FCSTD DOCUMENT  (FreeCAD 0.16R6712 (Git))
Label: randofo_robot_futaba_version
Comment: It has been modeled using a caliper and a real Futaba 3003 servo
License: CC-BY 3.0
LicenseURL: http://creativecommons.org/licenses/by/3.0/
objects: Part::Feature×186, Sketcher::SketchObject×36, PartDesign::Pocket×17, App::DocumentObjectGroup×13, Part::MultiFuse×12, PartDesign::Pad×10, Part::Fillet×4, Part::Cut×4, Mesh::Feature×4, Part::Loft×3, Part::Cylinder×3, Part::Extrusion×3, Part::Mirroring×2, Part::Compound×2, Part::Box×2, PartDesign::PolarPattern×1, PartDesign::Revolution×1, PartDesign::Fillet×1, PartDesign::Mirrored×1
note: 316 computed .brp shape members not serialized (recipe doc carries the construction recipe); baked Part::Feature solids carry a one-line shape summary decoded from their .brp

FEATURE [Sketcher::SketchObject] Sketch  label="body-sketch"
  Placement = pos=(0,0,0) rot=(1,0,0;1.5708rad)
  sketch-geometry (4):
    g0: LineSegment StartX=-20.15 StartY=36 StartZ=0 EndX=20.15 EndY=36 EndZ=0
    g1: LineSegment StartX=20.15 StartY=0 StartZ=0 EndX=-20.15 EndY=0 EndZ=0
    g2: LineSegment StartX=-20.15 StartY=0 StartZ=0 EndX=-20.15 EndY=36 EndZ=0
    g3: LineSegment StartX=20.15 StartY=36 StartZ=0 EndX=20.15 EndY=0 EndZ=0
  constraints (11):
    c: Coincident(g3,g1)
    c: Coincident(g1,g2)
    c: Horizontal(g0)
    c: Horizontal(g1)
    c: Vertical(g2)
    c: Symmetric(g0,g0,g-2)
    c: PointOnObject(g3,g-1)
    c: DistanceX(g0) = 40.3
    c: DistanceY(g0,g1) = -36
    c: Coincident(g2,g0)
    c: Coincident(g3,g0)
FEATURE [PartDesign::Pad] Pad  label="main_body"
  Length = 10
  Length2 = 100
  Placement = pos=(0,0,0) rot=(1,0,0;1.5708rad)
  Sketch = -> Sketch
  Type = 0
FEATURE [Sketcher::SketchObject] Sketch001  label="lateral-layer1-sketch"
  ExternalGeometry = -> [Pad]
  Placement = pos=(0,-10,0) rot=(1,0,0;1.5708rad)
  Support = -> Pad [Face14]
  sketch-geometry (6):
    g0: LineSegment StartX=20.15 StartY=33 StartZ=0 EndX=17.18 EndY=35.52 EndZ=0
    g1: LineSegment StartX=17.18 StartY=35.52 StartZ=0 EndX=-2.25 EndY=35.52 EndZ=0
    g2: LineSegment StartX=-2.25 StartY=35.52 StartZ=0 EndX=-20.15 EndY=33 EndZ=0
    g3: LineSegment StartX=-20.15 StartY=33 StartZ=0 EndX=-20.15 EndY=36 EndZ=0
    g4: LineSegment StartX=-20.15 StartY=36 StartZ=0 EndX=20.15 EndY=36 EndZ=0
    g5: LineSegment StartX=20.15 StartY=36 StartZ=0 EndX=20.15 EndY=33 EndZ=0
  constraints (16):
    c: Coincident(g0,g1)
    c: Horizontal(g1)
    c: Coincident(g1,g2)
    c: Coincident(g3,g2)
    c: Coincident(g4,g3)
    c: DistanceY(g0) = 33
    c: DistanceY(g4,g0) = -0.48
    c: DistanceX(g0,g0) = -2.97
    c: DistanceX(g4,g1) = -22.4
    c: Coincident(g5,g4)
    c: Coincident(g5,g0)
    c: PointOnObject(g0,g-4)
    c: Coincident(g4,g-4)
    c: Coincident(g3,g-3)
    c: PointOnObject(g2,g-3)
    c: DistanceY(g-1,g2) = 33
FEATURE [Sketcher::SketchObject] Sketch003
  Placement = pos=(0,0,0) rot=(0.57735,0.57735,0.57735;2.0944rad)
  sketch-geometry (4):
    g0: LineSegment StartX=-3.35 StartY=2.1 StartZ=0 EndX=3.35 EndY=2.1 EndZ=0
    g1: LineSegment StartX=3.35 StartY=2.1 StartZ=0 EndX=3.35 EndY=-2.1 EndZ=0
    g2: LineSegment StartX=3.35 StartY=-2.1 StartZ=0 EndX=-3.35 EndY=-2.1 EndZ=0
    g3: LineSegment StartX=-3.35 StartY=-2.1 StartZ=0 EndX=-3.35 EndY=2.1 EndZ=0
  constraints (12):
    c: Coincident(g0,g1)
    c: Coincident(g2,g3)
    c: Coincident(g3,g0)
    c: Horizontal(g0)
    c: Horizontal(g2)
    c: Vertical(g1)
    c: Vertical(g3)
    c: Symmetric(g0,g0,g-2)
    c: Coincident(g1,g2)
    c: DistanceY(g1) = -4.2
    c: DistanceX(g0) = 6.7
    c: Symmetric(g0,g2,g-1)
FEATURE [Sketcher::SketchObject] Sketch004
  Placement = pos=(1.8,0,0) rot=(0.57735,0.57735,0.57735;2.0944rad)
  sketch-geometry (4):
    g0: LineSegment StartX=-2.9 StartY=1.825 StartZ=0 EndX=2.9 EndY=1.825 EndZ=0
    g1: LineSegment StartX=2.9 StartY=1.825 StartZ=0 EndX=2.9 EndY=-1.825 EndZ=0
    g2: LineSegment StartX=2.9 StartY=-1.825 StartZ=0 EndX=-2.9 EndY=-1.825 EndZ=0
    g3: LineSegment StartX=-2.9 StartY=-1.825 StartZ=0 EndX=-2.9 EndY=1.825 EndZ=0
  constraints (12):
    c: Coincident(g0,g1)
    c: Coincident(g2,g3)
    c: Coincident(g3,g0)
    c: Horizontal(g0)
    c: Horizontal(g2)
    c: Vertical(g1)
    c: Vertical(g3)
    c: Symmetric(g0,g0,g-2)
    c: Coincident(g1,g2)
    c: DistanceY(g1) = -3.65
    c: DistanceX(g0) = 5.8
    c: Symmetric(g0,g2,g-1)
FEATURE [Part::Loft] Loft  label="wire-holder-body"
  Closed = false
  Placement = pos=(20.15,0,2.9) rot=(0,0,1;0rad)
  Ruled = false
  Sections = -> [Sketch003,Sketch004]
  Solid = true
FEATURE [Part::Cylinder] Cylinder  label="red-wire"
  Angle = 360
  Height = 10
  Placement = pos=(0,0,0) rot=(0,1,0;1.5708rad)
  Radius = 0.6
FEATURE [Part::Cylinder] Cylinder001  label="white-wire"
  Angle = 360
  Height = 10
  Placement = pos=(0,1.2,0) rot=(0,1,0;1.5708rad)
  Radius = 0.6
FEATURE [Part::Cylinder] Cylinder002  label="blck-wire"
  Angle = 360
  Height = 10
  Placement = pos=(0,-1.2,0) rot=(0,1,0;1.5708rad)
  Radius = 0.6
FEATURE [Sketcher::SketchObject] Sketch005
  ExternalGeometry = -> [Loft]
  Placement = pos=(21.95,0,2.9) rot=(0.57735,0.57735,0.57735;2.0944rad)
  Support = -> Loft [Face6]
  sketch-geometry (6):
    g0: LineSegment [constr] StartX=-1.2 StartY=0 StartZ=0 EndX=1.2 EndY=0 EndZ=0
    g1: ArcOfCircle CenterX=-1.2 CenterY=0 CenterZ=0 NormalX=0 NormalY=0 NormalZ=1 Radius=0.7 StartAngle=0.5411 EndAngle=5.74209
    g2: ArcOfCircle CenterX=0 CenterY=0 CenterZ=0 NormalX=0 NormalY=0 NormalZ=1 Radius=0.7 StartAngle=0.5411 EndAngle=2.60049
    g3: ArcOfCircle CenterX=0 CenterY=0 CenterZ=0 NormalX=0 NormalY=0 NormalZ=1 Radius=0.7 StartAngle=3.68269 EndAngle=5.74209
    g4: ArcOfCircle CenterX=1.2 CenterY=0 CenterZ=0 NormalX=0 NormalY=0 NormalZ=1 Radius=0.7 StartAngle=3.68269 EndAngle=8.88368
    g5: LineSegment [constr] StartX=-1.2 StartY=0 StartZ=0 EndX=-1.2 EndY=-0.7 EndZ=0
  constraints (20):
    c: Horizontal(g0)
    c: Symmetric(g0,g0,g-2)
    c: Coincident(g1,g0)
    c: PointOnObject(g2,g0)
    c: Coincident(g2,g1)
    c: PointOnObject(g2,g-2)
    c: Coincident(g3,g2)
    c: Coincident(g3,g1)
    c: Coincident(g4,g0)
    c: Coincident(g4,g2)
    c: Coincident(g4,g3)
    c: Equal(g1,g2)
    c: Equal(g2,g4)
    c: Equal(g4,g3)
    c: DistanceX(g2,g0) = 1.2
    c: Coincident(g5,g0)
    c: Vertical(g5)
    c: PointOnObject(g5,g1)
    c: Radius(g4) = 0.7
    c: PointOnObject(g0,g-1)
FEATURE [PartDesign::Pocket] Pocket002  label="wire-holder"
  Length = 1
  Placement = pos=(20.15,0,2.9) rot=(0,0,1;0rad)
  Sketch = -> Sketch005
  Type = 0
FEATURE [App::DocumentObjectGroup] Group  label="servo-wire-holder"
  Group = -> [Pocket002,Loft]
FEATURE [PartDesign::Pocket] Pocket  label="lateral-layer1"
  Length = 0.8
  Placement = pos=(0,0,0) rot=(1,0,0;1.5708rad)
  Sketch = -> Sketch001
  Type = 0
FEATURE [Sketcher::SketchObject] Sketch002  label="lateral-layer2-sketch"
  Placement = pos=(0,-9.2,0) rot=(1,0,0;1.5708rad)
  Support = -> Pocket [Face4]
  sketch-geometry (12):
    g0: GeomPoint [constr] X=19.55 Y=33.5091 Z=0
    g1: GeomPoint [constr] X=18.65 Y=36 Z=0
    g2: LineSegment StartX=18.65 StartY=36 StartZ=0 EndX=19.55 EndY=33.5091 EndZ=0
    g3: LineSegment StartX=19.55 StartY=33.5091 StartZ=0 EndX=20.15 EndY=33 EndZ=0
    g4: LineSegment StartX=18.65 StartY=36 StartZ=0 EndX=20.15 EndY=36 EndZ=0
    g5: LineSegment StartX=20.15 StartY=36 StartZ=0 EndX=20.15 EndY=33 EndZ=0
    g6: GeomPoint [constr] X=-16.9 Y=33.4575 Z=0
    g7: GeomPoint [constr] X=-13.35 Y=36 Z=0
    g8: LineSegment StartX=-20.15 StartY=33 StartZ=0 EndX=-16.9 EndY=33.4575 EndZ=0
    g9: LineSegment StartX=-16.9 StartY=33.4575 StartZ=0 EndX=-13.35 EndY=36 EndZ=0
    g10: LineSegment StartX=-20.15 StartY=33 StartZ=0 EndX=-20.15 EndY=36 EndZ=0
    g11: LineSegment StartX=-20.15 StartY=36 StartZ=0 EndX=-13.35 EndY=36 EndZ=0
  constraints (16):
    c: Coincident(g2,g1)
    c: Coincident(g2,g0)
    c: Coincident(g4,g1)
    c: Coincident(g5,g4)
    c: Coincident(g5,g3)
    c: Coincident(g3,g0)
    c: Coincident(g8,g6)
    c: Coincident(g9,g6)
    c: Coincident(g9,g7)
    c: DistanceX(g8,g6) = 3.25
    c: DistanceX(g7,g4) = 33.5
    c: Coincident(g10,g8)
    c: Coincident(g11,g10)
    c: Coincident(g11,g7)
    c: DistanceX(g4,g0) = -0.6
    c: DistanceX(g1,g4) = 1.5
FEATURE [PartDesign::Pocket] Pocket003  label="lateral-layer2"
  Length = 5
  Placement = pos=(0,0,0) rot=(1,0,0;1.5708rad)
  Sketch = -> Sketch002
  Type = 1
FEATURE [Part::Mirroring] Part__Mirroring  label="lateral-layer2 (Mirror #1)"
  Base = (0,0,0)
  Normal = (0,1,0)
  Source = -> Pocket003
FEATURE [Sketcher::SketchObject] Sketch006  label="ear-body-sketch"
  sketch-geometry (4):
    g0: LineSegment StartX=-27.75 StartY=9.05 StartZ=0 EndX=27.75 EndY=9.05 EndZ=0
    g1: LineSegment StartX=27.75 StartY=9.05 StartZ=0 EndX=27.75 EndY=-9.05 EndZ=0
    g2: LineSegment StartX=27.75 StartY=-9.05 StartZ=0 EndX=-27.75 EndY=-9.05 EndZ=0
    g3: LineSegment StartX=-27.75 StartY=-9.05 StartZ=0 EndX=-27.75 EndY=9.05 EndZ=0
  constraints (11):
    c: Coincident(g0,g1)
    c: Coincident(g1,g2)
    c: Coincident(g2,g3)
    c: Coincident(g3,g0)
    c: Horizontal(g0)
    c: Horizontal(g2)
    c: Vertical(g1)
    c: Vertical(g3)
    c: Symmetric(g0,g1,g-1)
    c: DistanceX(g0) = 55.5
    c: DistanceY(g1) = -18.1
FEATURE [PartDesign::Pad] Pad001  label="ear-body"
  Length = 2.6
  Length2 = 100
  Sketch = -> Sketch006
  Type = 0
FEATURE [Sketcher::SketchObject] Sketch007  label="ear-holes-sketch"
  Placement = pos=(0,0,2.6) rot=(0,0,1;0rad)
  Support = -> Pad001 [Face6]
  sketch-geometry (12):
    g0: Circle CenterX=-24.45 CenterY=5.05 CenterZ=0 NormalX=0 NormalY=0 NormalZ=1 Radius=2.15
    g1: Circle CenterX=-24.45 CenterY=-5.05 CenterZ=0 NormalX=0 NormalY=0 NormalZ=1 Radius=2.15
    g2: Circle CenterX=24.45 CenterY=5.05 CenterZ=0 NormalX=0 NormalY=0 NormalZ=1 Radius=2.15
    g3: Circle CenterX=24.45 CenterY=-5.05 CenterZ=0 NormalX=0 NormalY=0 NormalZ=1 Radius=2.15
    g4: LineSegment [constr] StartX=-24.45 StartY=5.05 StartZ=0 EndX=24.45 EndY=5.05 EndZ=0
    g5: LineSegment [constr] StartX=24.45 StartY=5.05 StartZ=0 EndX=24.45 EndY=-5.05 EndZ=0
    g6: LineSegment [constr] StartX=24.45 StartY=-5.05 StartZ=0 EndX=-24.45 EndY=-5.05 EndZ=0
    g7: LineSegment [constr] StartX=-24.45 StartY=-5.05 StartZ=0 EndX=-24.45 EndY=5.05 EndZ=0
    g8: GeomPoint [constr] X=-24.45 Y=2.9 Z=0
    g9: GeomPoint [constr] X=-22.3 Y=5.05 Z=0
    g10: GeomPoint [constr] X=-24.45 Y=-2.9 Z=0
    g11: GeomPoint [constr] X=22.3 Y=5.05 Z=0
  constraints (27):
    c: Coincident(g4,g5)
    c: Coincident(g5,g6)
    c: Coincident(g6,g7)
    c: Coincident(g7,g4)
    c: Horizontal(g4)
    c: Horizontal(g6)
    c: Vertical(g5)
    c: Vertical(g7)
    c: Symmetric(g4,g5,g-1)
    c: Coincident(g2,g4)
    c: Coincident(g3,g5)
    c: Coincident(g1,g6)
    c: Coincident(g0,g4)
    c: PointOnObject(g8,g7)
    c: PointOnObject(g9,g4)
    c: PointOnObject(g8,g0)
    c: PointOnObject(g9,g0)
    c: Equal(g0,g1)
    c: Equal(g1,g2)
    c: Equal(g2,g3)
    c: Radius(g0) = 2.15
    c: PointOnObject(g10,g7)
    c: PointOnObject(g10,g1)
    c: DistanceY(g8,g10) = -5.8
    c: PointOnObject(g11,g4)
    c: PointOnObject(g11,g2)
    c: DistanceX(g9,g11) = 44.6
FEATURE [PartDesign::Pocket] Pocket004  label="ear-holes"
  Length = 5
  Sketch = -> Sketch007
  Type = 1
FEATURE [Sketcher::SketchObject] Sketch008  label="nose-sketch"
  Placement = pos=(0,0,2.6) rot=(1,0,0;1.5708rad)
  sketch-geometry (6):
    g0: LineSegment StartX=-24.1 StartY=0 StartZ=0 EndX=-23.23 EndY=0.6 EndZ=0
    g1: LineSegment StartX=-23.23 StartY=0.6 StartZ=0 EndX=-20.15 EndY=1.5 EndZ=0
    g2: LineSegment StartX=-20.15 StartY=1.5 StartZ=0 EndX=20.15 EndY=1.5 EndZ=0
    g3: LineSegment StartX=20.15 StartY=1.5 StartZ=0 EndX=23.23 EndY=0.6 EndZ=0
    g4: LineSegment StartX=23.23 StartY=0.6 StartZ=0 EndX=24.1 EndY=0 EndZ=0
    g5: LineSegment StartX=24.1 StartY=0 StartZ=0 EndX=-24.1 EndY=0 EndZ=0
  constraints (17):
    c: PointOnObject(g0,g-1)
    c: Coincident(g0,g1)
    c: Coincident(g1,g2)
    c: Horizontal(g2)
    c: Coincident(g2,g3)
    c: Coincident(g3,g4)
    c: PointOnObject(g4,g-1)
    c: Coincident(g4,g5)
    c: Coincident(g5,g0)
    c: DistanceX(g2) = 40.3
    c: Symmetric(g1,g2,g-2)
    c: Symmetric(g3,g0,g-2)
    c: Symmetric(g0,g4,g-2)
    c: DistanceX(g0,g4) = 48.2
    c: DistanceX(g0,g1) = 3.08
    c: DistanceY(g0,g1) = 1.5
    c: DistanceY(g0,g0) = -0.6
FEATURE [PartDesign::Pad] Pad002  label="nose"
  Length = 1.5
  Length2 = 100
  Midplane = true
  Placement = pos=(0,0,2.6) rot=(1,0,0;1.5708rad)
  Sketch = -> Sketch008
  Type = 0
FEATURE [Sketcher::SketchObject] Sketch010
  sketch-geometry (1):
    g0: Circle CenterX=0 CenterY=0 CenterZ=0 NormalX=0 NormalY=0 NormalZ=1 Radius=7.2
  constraints (2):
    c: Coincident(g0,g-1)
    c: Radius(g0) = 7.2
FEATURE [Sketcher::SketchObject] Sketch011
  Placement = pos=(0,0,1.3) rot=(0,0,1;0rad)
  sketch-geometry (1):
    g0: Circle CenterX=0 CenterY=0 CenterZ=0 NormalX=0 NormalY=0 NormalZ=1 Radius=5.625
  constraints (2):
    c: Coincident(g0,g-1)
    c: Radius(g0) = 5.625
FEATURE [Part::Loft] Loft001  label="shaft-base1"
  Closed = false
  Placement = pos=(9.45,0,36) rot=(0,0,1;0rad)
  Ruled = false
  Sections = -> [Sketch010,Sketch011]
  Solid = true
FEATURE [Sketcher::SketchObject] Sketch012
  Placement = pos=(9.45,0,37.3) rot=(0,0,1;0rad)
  Support = -> Loft001 [Face3]
  sketch-geometry (1):
    g0: Circle CenterX=0 CenterY=0 CenterZ=0 NormalX=0 NormalY=0 NormalZ=1 Radius=4.95
  constraints (2):
    c: Coincident(g0,g-1)
    c: Radius(g0) = 4.95
FEATURE [PartDesign::Pad] Pad005  label="shaft-base2"
  Length = 0.2
  Length2 = 100
  Placement = pos=(9.45,0,36) rot=(0,0,1;0rad)
  Sketch = -> Sketch012
  Type = 0
FEATURE [Sketcher::SketchObject] Sketch013
  Placement = pos=(9.45,0,37.5) rot=(0,0,1;0rad)
  Support = -> Pad005 [Face5]
  sketch-geometry (1):
    g0: Circle CenterX=0 CenterY=0 CenterZ=0 NormalX=0 NormalY=0 NormalZ=1 Radius=3
  constraints (2):
    c: Coincident(g0,g-1)
    c: Radius(g0) = 3
FEATURE [PartDesign::Pad] Pad006  label="base-plus-basic-shaft"
  Length = 4.24
  Length2 = 100
  Placement = pos=(9.45,0,36) rot=(0,0,1;0rad)
  Sketch = -> Sketch013
  Type = 0
FEATURE [Sketcher::SketchObject] Sketch014  label="master-tooth-sketch"
  ExternalGeometry = -> [Pad006]
  Placement = pos=(9.45,0,41.74) rot=(0,0,1;0rad)
  Support = -> Pad006 [Face7]
  sketch-geometry (8):
    g0: Circle [constr] CenterX=0 CenterY=0 CenterZ=0 NormalX=0 NormalY=0 NormalZ=1 Radius=3.2
    g1: Circle [constr] CenterX=0 CenterY=0 CenterZ=0 NormalX=0 NormalY=0 NormalZ=1 Radius=2.8
    g2: LineSegment StartX=-0.1 StartY=3.19844 StartZ=0 EndX=0.1 EndY=3.19844 EndZ=0
    g3: LineSegment [constr] StartX=-0.1 StartY=3.19844 StartZ=0 EndX=0 EndY=0 EndZ=0
    g4: LineSegment [constr] StartX=0.1 StartY=3.19844 StartZ=0 EndX=0 EndY=0 EndZ=0
    g5: LineSegment StartX=-0.1 StartY=3.19844 StartZ=0 EndX=-0.0875 EndY=2.79863 EndZ=0
    g6: LineSegment StartX=-0.0875 StartY=2.79863 StartZ=0 EndX=0.0875 EndY=2.79863 EndZ=0
    g7: LineSegment StartX=0.0875 StartY=2.79863 StartZ=0 EndX=0.1 EndY=3.19844 EndZ=0
  constraints (20):
    c: Coincident(g0,g-1)
    c: Radius(g0) = 3.2
    c: Coincident(g1,g-1)
    c: Radius(g1) = 2.8
    c: Horizontal(g2)
    c: PointOnObject(g2,g0)
    c: PointOnObject(g2,g0)
    c: DistanceX(g2,g2) = 0.2
    c: Coincident(g3,g2)
    c: Coincident(g2,g4)
    c: Coincident(g4,g-1)
    c: Coincident(g3,g-1)
    c: Coincident(g5,g6)
    c: Coincident(g6,g7)
    c: Coincident(g5,g2)
    c: Coincident(g7,g2)
    c: PointOnObject(g5,g3)
    c: PointOnObject(g6,g4)
    c: PointOnObject(g5,g1)
    c: PointOnObject(g6,g1)
FEATURE [PartDesign::Pocket] Pocket005  label="master-tooth"
  Length = 4.1
  Placement = pos=(9.45,0,36) rot=(0,0,1;0rad)
  Sketch = -> Sketch014
  Type = 0
FEATURE [PartDesign::PolarPattern] PolarPattern  label="shaft-teeth"
  Angle = 360
  Axis = -> Sketch014 [N_Axis]
  Occurrences = 36
  Originals = -> [Pocket005]
  Placement = pos=(9.45,0,36) rot=(0,0,1;0rad)
FEATURE [Sketcher::SketchObject] Sketch017  label="top-cone-top"
  sketch-geometry (1):
    g0: Circle CenterX=0 CenterY=0 CenterZ=0 NormalX=0 NormalY=0 NormalZ=1 Radius=1.1
  constraints (2):
    c: Coincident(g0,g-1)
    c: Radius(g0) = 1.1
FEATURE [Sketcher::SketchObject] Sketch018  label="top-cone-bottom"
  Placement = pos=(0,0,0.6) rot=(0,0,1;0rad)
  sketch-geometry (1):
    g0: Circle CenterX=0 CenterY=0 CenterZ=0 NormalX=0 NormalY=0 NormalZ=1 Radius=1.25
  constraints (2):
    c: Coincident(g0,g-1)
    c: Radius(g0) = 1.25
FEATURE [Sketcher::SketchObject] Sketch021
  Placement = pos=(0,0,0) rot=(1,0,0;1.5708rad)
  sketch-geometry (6):
    g0: LineSegment StartX=0 StartY=0 StartZ=0 EndX=0.81 EndY=0 EndZ=0
    g1: LineSegment StartX=0.81 StartY=0 StartZ=0 EndX=0.81 EndY=27.6 EndZ=0
    g2: LineSegment StartX=0 StartY=28.9 StartZ=0 EndX=0 EndY=0 EndZ=0
    g3: LineSegment StartX=0.81 StartY=27.6 StartZ=0 EndX=1.65 EndY=27.6 EndZ=0
    g4: LineSegment StartX=1.65 StartY=27.6 StartZ=0 EndX=1.65 EndY=28.9 EndZ=0
    g5: LineSegment StartX=1.65 StartY=28.9 StartZ=0 EndX=0 EndY=28.9 EndZ=0
  constraints (17):
    c: Coincident(g0,g1)
    c: Coincident(g2,g0)
    c: Horizontal(g0)
    c: Vertical(g1)
    c: Vertical(g2)
    c: Coincident(g0,g-1)
    c: Coincident(g3,g4)
    c: Coincident(g4,g5)
    c: Coincident(g2,g5)
    c: Horizontal(g5)
    c: Coincident(g3,g1)
    c: Horizontal(g3)
    c: Vertical(g4)
    c: DistanceY(g2) = -28.9
    c: DistanceX(g0) = 0.81
    c: DistanceX(g5) = -1.65
    c: DistanceY(g4) = 1.3
FEATURE [PartDesign::Revolution] Revolution  label="screw-shape"
  Angle = 360
  Axis = (0,0,1)
  Base = (0,0,0)
  Placement = pos=(0,0,0) rot=(1,0,0;1.5708rad)
  ReferenceAxis = -> Sketch021 [V_Axis]
  Reversed = true
  Sketch = -> Sketch021
FEATURE [Sketcher::SketchObject] Sketch022  label="screw-cross-sketch"
  Placement = pos=(0,0,28.9) rot=(0,0,1;3.14159rad)
  Support = -> Revolution [Face5]
  sketch-geometry (12):
    g0: LineSegment StartX=-0.3 StartY=0.75 StartZ=0 EndX=0.3 EndY=0.75 EndZ=0
    g1: LineSegment StartX=0.3 StartY=0.75 StartZ=0 EndX=0.3 EndY=0.3 EndZ=0
    g2: LineSegment StartX=0.3 StartY=-0.75 StartZ=0 EndX=-0.3 EndY=-0.75 EndZ=0
    g3: LineSegment StartX=-0.3 StartY=-0.75 StartZ=0 EndX=-0.3 EndY=-0.3 EndZ=0
    g4: LineSegment StartX=-0.75 StartY=0.3 StartZ=0 EndX=-0.3 EndY=0.3 EndZ=0
    g5: LineSegment StartX=0.75 StartY=0.3 StartZ=0 EndX=0.75 EndY=-0.3 EndZ=0
    g6: LineSegment StartX=0.75 StartY=-0.3 StartZ=0 EndX=0.3 EndY=-0.3 EndZ=0
    g7: LineSegment StartX=-0.75 StartY=-0.3 StartZ=0 EndX=-0.75 EndY=0.3 EndZ=0
    g8: LineSegment StartX=-0.3 StartY=0.3 StartZ=0 EndX=-0.3 EndY=0.75 EndZ=0
    g9: LineSegment StartX=0.3 StartY=-0.3 StartZ=0 EndX=0.3 EndY=-0.75 EndZ=0
    g10: LineSegment StartX=0.3 StartY=0.3 StartZ=0 EndX=0.75 EndY=0.3 EndZ=0
    g11: LineSegment StartX=-0.3 StartY=-0.3 StartZ=0 EndX=-0.75 EndY=-0.3 EndZ=0
  constraints (30):
    c: Coincident(g0,g1)
    c: Coincident(g9,g2)
    c: Coincident(g2,g3)
    c: Coincident(g8,g0)
    c: Horizontal(g0)
    c: Horizontal(g2)
    c: Vertical(g1)
    c: Vertical(g3)
    c: Symmetric(g0,g9,g-1)
    c: Coincident(g10,g5)
    c: Coincident(g5,g6)
    c: Coincident(g11,g7)
    c: Coincident(g7,g4)
    c: Horizontal(g4)
    c: Horizontal(g6)
    c: Vertical(g5)
    c: Vertical(g7)
    c: Symmetric(g4,g5,g-1)
    c: Tangent(g3,g8)
    c: Tangent(g1,g9)
    c: Coincident(g4,g8)
    c: Coincident(g10,g1)
    c: Tangent(g4,g10)
    c: Coincident(g6,g9)
    c: Coincident(g11,g3)
    c: Tangent(g6,g11)
    c: Equal(g0,g7)
    c: Equal(g8,g4)
    c: DistanceX(g4,g5) = 1.5
    c: DistanceX(g0) = 0.6
FEATURE [PartDesign::Pocket] Pocket002006
  Length = 0.5
  Placement = pos=(0,0,0) rot=(1,0,0;1.5708rad)
  Sketch = -> Sketch022
  Type = 0
FEATURE [PartDesign::Fillet] Fillet  label="servo-screw-final1"
  Base = -> Pocket002006 [Edge5]
  Placement = pos=(0,0,0) rot=(1,0,0;1.5708rad)
  Radius = 0.4
FEATURE [Part::Feature] Fillet001  label="servo-screw1"
  Placement = pos=(17.6429,-7.49289,29) rot=(-1,0,0;1.5708rad)
  shape: bbox 3.572 x 3.572 x 28.9 mm, 19 faces (baked)
FEATURE [Part::Feature] Fillet001001  label="servo-screw002"
  Placement = pos=(-17.6429,-7.49289,29) rot=(-1,0,0;1.5708rad)
  shape: bbox 3.572 x 3.572 x 28.9 mm, 19 faces (baked)
FEATURE [Part::Feature] Fillet001002  label="servo-screw003"
  Placement = pos=(-17.6429,7.49289,29) rot=(-1,0,0;1.5708rad)
  shape: bbox 3.572 x 3.572 x 28.9 mm, 19 faces (baked)
FEATURE [Part::Feature] Fillet001003  label="servo-screw004"
  Placement = pos=(17.6429,7.49289,29) rot=(-1,0,0;1.5708rad)
  shape: bbox 3.572 x 3.572 x 28.9 mm, 19 faces (baked)
FEATURE [Sketcher::SketchObject] Sketch023
  Placement = pos=(9.45,0,41.74) rot=(0,0,1;0rad)
  Support = -> PolarPattern [Face9]
  sketch-geometry (1):
    g0: Circle CenterX=0 CenterY=0 CenterZ=0 NormalX=0 NormalY=0 NormalZ=1 Radius=0.9
  constraints (2):
    c: Coincident(g0,g-1)
    c: Radius(g0) = 0.9
FEATURE [PartDesign::Pocket] Pocket002007  label="shaft-drill-1"
  Length = 3
  Placement = pos=(9.45,0,36) rot=(0,0,1;0rad)
  Sketch = -> Sketch023
  Type = 0
FEATURE [Sketcher::SketchObject] Sketch024
  Placement = pos=(9.45,0,41.74) rot=(0,0,1;0rad)
  Support = -> Pocket002007 [Face9]
  sketch-geometry (1):
    g0: Circle CenterX=0 CenterY=0 CenterZ=0 NormalX=0 NormalY=0 NormalZ=1 Radius=1.15
  constraints (2):
    c: Coincident(g0,g-1)
    c: Radius(g0) = 1.15
FEATURE [PartDesign::Pocket] Pocket002008  label="shaft-drill-2"
  Length = 1
  Placement = pos=(9.45,0,36) rot=(0,0,1;0rad)
  Sketch = -> Sketch024
  Type = 0
FEATURE [App::DocumentObjectGroup] Group002  label="servo-shaft"
  Group = -> [Loft001,Pad005,Pad006,Pocket005,PolarPattern,Pocket002007,Pocket002008]
FEATURE [Part::Loft] Loft002  label="top-cone-master"
  Closed = false
  Placement = pos=(1,5.6,35.5) rot=(0,0,1;0rad)
  Ruled = false
  Sections = -> [Sketch017,Sketch018]
  Solid = true
FEATURE [Part::MultiFuse] Fusion006  label="servo-body001"
  Shapes = -> [Pocket003,Part__Mirroring]
FEATURE [Sketcher::SketchObject] Sketch015  label="top-details-1-sketch"
  ExternalGeometry = -> [Fusion006]
  Placement = pos=(0,0,36) rot=(0,0,1;0rad)
  Support = -> Fusion006 [Face8]
  sketch-geometry (10):
    g0: ArcOfCircle CenterX=-2.25 CenterY=0 CenterZ=0 NormalX=0 NormalY=0 NormalZ=1 Radius=1.7 StartAngle=4.71239 EndAngle=7.85398
    g1: LineSegment StartX=-2.25 StartY=9.2 StartZ=0 EndX=-2.25 EndY=1.7 EndZ=0
    g2: LineSegment StartX=-2.25 StartY=-1.7 StartZ=0 EndX=-2.25 EndY=-9.2 EndZ=0
    g3: ArcOfCircle CenterX=-2.25 CenterY=0 CenterZ=0 NormalX=0 NormalY=0 NormalZ=1 Radius=2.6 StartAngle=5.06586 EndAngle=7.50051
    g4: LineSegment [constr] StartX=-0.55 StartY=0 StartZ=0 EndX=0.35 EndY=0 EndZ=0
    g5: LineSegment [constr] StartX=-1.35 StartY=2.43926 StartZ=0 EndX=-2.25 EndY=2.43926 EndZ=0
    g6: LineSegment StartX=-1.35 StartY=2.43926 StartZ=0 EndX=-1.35 EndY=9.2 EndZ=0
    g7: LineSegment StartX=-2.25 StartY=9.2 StartZ=0 EndX=-1.35 EndY=9.2 EndZ=0
    g8: LineSegment StartX=-1.35 StartY=-2.43926 StartZ=0 EndX=-1.35 EndY=-9.2 EndZ=0
    g9: LineSegment StartX=-2.25 StartY=-9.2 StartZ=0 EndX=-1.35 EndY=-9.2 EndZ=0
  constraints (30):
    c: Radius(g0) = 1.7
    c: Symmetric(g0,g0,g-1)
    c: Coincident(g1,g0)
    c: Vertical(g1)
    c: Vertical(g2)
    c: Coincident(g2,g0)
    c: PointOnObject(g0,g1)
    c: Symmetric(g3,g3,g-1)
    c: PointOnObject(g4,g-1)
    c: Horizontal(g4)
    c: PointOnObject(g4,g0)
    c: PointOnObject(g4,g3)
    c: Coincident(g3,g0)
    c: DistanceX(g4) = 0.9
    c: Horizontal(g5)
    c: PointOnObject(g5,g1)
    c: Vertical(g6)
    c: Horizontal(g7)
    c: Coincident(g7,g1)
    c: Coincident(g7,g6)
    c: Coincident(g6,g3)
    c: DistanceX(g5) = -0.9
    c: Coincident(g5,g3)
    c: Coincident(g8,g3)
    c: Vertical(g8)
    c: Coincident(g9,g2)
    c: Horizontal(g9)
    c: Coincident(g9,g8)
    c: Symmetric(g1,g2,g-1)
    c: Coincident(g1,g-3)
FEATURE [PartDesign::Pocket] Pocket002008004  label="top-details-1"
  Length = 0.48
  Sketch = -> Sketch015
  Type = 0
FEATURE [Sketcher::SketchObject] Sketch016  label="top-details-2-sketch"
  ExternalGeometry = -> [Pocket002008004]
  Placement = pos=(0,0,36) rot=(0,0,1;0rad)
  Support = -> Pocket002008004 [Face21]
  sketch-geometry (6):
    g0: LineSegment StartX=-12.35 StartY=8.2 StartZ=0 EndX=-3.25 EndY=8.2 EndZ=0
    g1: LineSegment StartX=-3.25 StartY=8.2 StartZ=0 EndX=-3.25 EndY=-8.2 EndZ=0
    g2: LineSegment StartX=-3.25 StartY=-8.2 StartZ=0 EndX=-12.35 EndY=-8.2 EndZ=0
    g3: LineSegment StartX=-12.35 StartY=-8.2 StartZ=0 EndX=-12.35 EndY=8.2 EndZ=0
    g4: LineSegment [constr] StartX=-13.35 StartY=9.2 StartZ=0 EndX=-12.35 EndY=8.2 EndZ=0
    g5: LineSegment [constr] StartX=-2.25 StartY=-9.2 StartZ=0 EndX=-3.25 EndY=-8.2 EndZ=0
  constraints (16):
    c: Coincident(g4,g0)
    c: Coincident(g0,g3)
    c: Horizontal(g0)
    c: Vertical(g3)
    c: Coincident(g0,g1)
    c: Vertical(g1)
    c: Coincident(g2,g3)
    c: Horizontal(g2)
    c: Coincident(g1,g2)
    c: Coincident(g5,g1)
    c: DistanceX(g0,g4) = -1
    c: DistanceX(g5,g1) = -1
    c: Coincident(g4,g-3)
    c: Angle(g-3,g4) = 0.785398
    c: Coincident(g5,g-4)
    c: Angle(g5,g-1) = 0.785398
FEATURE [PartDesign::Pocket] Pocket002008007002  label="top-details-2"
  Length = 0.1
  Sketch = -> Sketch016
  Type = 0
FEATURE [Sketcher::SketchObject] Sketch025  label="bottom-details-1-sketch"
  ExternalGeometry = -> [Pocket002008007002]
  Placement = pos=(0,0,0) rot=(1,0,0;3.14159rad)
  Support = -> Pocket002008007002 [Face17]
  sketch-geometry (12):
    g0: LineSegment StartX=-17.6429 StartY=5.6 StartZ=0 EndX=-20.15 EndY=5.6 EndZ=0
    g1: LineSegment StartX=-20.15 StartY=5.6 StartZ=0 EndX=-20.15 EndY=10 EndZ=0
    g2: LineSegment StartX=-15.75 StartY=10 StartZ=0 EndX=-15.75 EndY=7.49289 EndZ=0
    g3: ArcOfCircle CenterX=-17.6429 CenterY=7.49289 CenterZ=0 NormalX=0 NormalY=0 NormalZ=1 Radius=1.89289 StartAngle=4.7124 EndAngle=6.28319
    g4: Circle [constr] CenterX=-17.6429 CenterY=7.49289 CenterZ=0 NormalX=0 NormalY=0 NormalZ=1 Radius=1
    g5: LineSegment StartX=-20.15 StartY=10 StartZ=0 EndX=-15.75 EndY=10 EndZ=0
    g6: LineSegment [constr] StartX=-20.15 StartY=10 StartZ=0 EndX=-18.35 EndY=8.2 EndZ=0
    g7: LineSegment StartX=-20.15 StartY=-5.6 StartZ=0 EndX=-20.15 EndY=-10 EndZ=0
    g8: LineSegment StartX=-20.15 StartY=-5.6 StartZ=0 EndX=-17.6429 EndY=-5.6 EndZ=0
    g9: LineSegment StartX=-20.15 StartY=-10 StartZ=0 EndX=-15.75 EndY=-10 EndZ=0
    g10: LineSegment StartX=-15.75 StartY=-10 StartZ=0 EndX=-15.75 EndY=-7.49289 EndZ=0
    g11: ArcOfCircle CenterX=-17.6429 CenterY=-7.49289 CenterZ=0 NormalX=0 NormalY=0 NormalZ=1 Radius=1.89289 StartAngle=6.28318 EndAngle=7.85397
  constraints (34):
    c: Coincident(g0,g1)
    c: Vertical(g2)
    c: Horizontal(g0)
    c: Vertical(g1)
    c: Coincident(g3,g2)
    c: Coincident(g3,g0)
    c: Tangent(g3,g0)
    c: Radius(g4) = 1
    c: Coincident(g3,g4)
    c: Coincident(g5,g1)
    c: Coincident(g5,g2)
    c: Horizontal(g5)
    c: Coincident(g6,g1)
    c: Angle(g6,g5) = 0.785398
    c: PointOnObject(g6,g4)
    c: PointOnObject(g3,g6)
    c: DistanceX(g5) = 4.4
    c: DistanceX(g6,g1) = -1.8
    c: Coincident(g1,g-3)
    c: Tangent(g2,g3)
    c: Vertical(g7)
    c: Symmetric(g7,g1,g-1)
    c: Symmetric(g7,g0,g-1)
    c: Horizontal(g8)
    c: Coincident(g8,g7)
    c: Symmetric(g8,g0,g-1)
    c: Horizontal(g9)
    c: Coincident(g9,g7)
    c: Symmetric(g9,g2,g-1)
    c: Coincident(g10,g9)
    c: Symmetric(g10,g2,g-1)
    c: Coincident(g11,g8)
    c: Coincident(g11,g10)
    c: Symmetric(g11,g3,g-1)
FEATURE [PartDesign::Pocket] Pocket002008007003  label="bottom-details-1"
  Length = 1.4
  Sketch = -> Sketch025
  Type = 0
FEATURE [PartDesign::Mirrored] Mirrored  label="bottom-details-1-complete"
  MirrorPlane = -> Sketch025 [V_Axis]
  Originals = -> [Pocket002008007003]
FEATURE [Sketcher::SketchObject] Sketch026  label="bottom-drills-sketch"
  ExternalGeometry = -> [Mirrored]
  Placement = pos=(0,0,0) rot=(1,0,0;3.14159rad)
  Support = -> Mirrored [Face19]
  sketch-geometry (6):
    g0: Circle CenterX=-17.6429 CenterY=7.49289 CenterZ=0 NormalX=0 NormalY=0 NormalZ=1 Radius=1
    g1: LineSegment [constr] StartX=-20.15 StartY=10 StartZ=0 EndX=-18.35 EndY=8.2 EndZ=0
    g2: LineSegment [constr] StartX=-20.15 StartY=10 StartZ=0 EndX=0 EndY=10 EndZ=0
    g3: Circle CenterX=-17.6429 CenterY=-7.49289 CenterZ=0 NormalX=0 NormalY=0 NormalZ=1 Radius=1
    g4: Circle CenterX=17.6429 CenterY=7.49289 CenterZ=0 NormalX=0 NormalY=0 NormalZ=1 Radius=1
    g5: Circle CenterX=17.6429 CenterY=-7.49289 CenterZ=0 NormalX=0 NormalY=0 NormalZ=1 Radius=1
  constraints (15):
    c: Radius(g0) = 1
    c: Coincident(g2,g1)
    c: Horizontal(g2)
    c: PointOnObject(g2,g-2)
    c: Angle(g1,g2) = 0.785398
    c: PointOnObject(g1,g0)
    c: PointOnObject(g0,g1)
    c: Coincident(g1,g-3)
    c: DistanceX(g1,g1) = -1.8
    c: Equal(g0,g3)
    c: Equal(g3,g5)
    c: Equal(g5,g4)
    c: Symmetric(g0,g3,g-1)
    c: Symmetric(g0,g4,g-2)
    c: Symmetric(g0,g5,g-1)
FEATURE [PartDesign::Pocket] Pocket002008007004  label="servo-body-final-1"
  Length = 30
  Sketch = -> Sketch026
  Type = 0
FEATURE [Part::Fillet] Fillet001007  label="servo-body-final-rounded"
  Base = -> Pocket002008007004
  Edges = 24 edges r=0.6: [Edge2,Edge5,Edge18,Edge24,Edge25,Edge26,Edge29,Edge30,Edge32,Edge33,Edge36,Edge39,Edge40,Edge41,Edge43,Edge46,Edge52,Edge53,Edge56,Edge59,Edge62,Edge77,Edge93,Edge95]
FEATURE [App::DocumentObjectGroup] Group005  label="servo-body"
  Group = -> [Pad,Pocket,Fusion006,Pocket002008004,Pocket002008007002,Pocket002008007003,Mirrored,Pocket002008007004,Fillet001007]
FEATURE [Part::MultiFuse] Fusion001  label="ears-final"
  Placement = pos=(0,0,25.8) rot=(0,0,1;0rad)
  Shapes = -> [Pocket004,Pad002]
FEATURE [Part::Fillet] Fillet001008  label="ears-final-rounded"
  Base = -> Fusion001
  Edges = 4 edges r=0.6: [Edge1,Edge2,Edge5,Edge8]
FEATURE [App::DocumentObjectGroup] Group001  label="servo-ears"
  Group = -> [Pad001,Pocket004,Pad002,Fusion001,Fillet001008]
FEATURE [Part::Feature] Fillet001007001  label="servo-body-1"
  shape: bbox 40.3 x 20 x 36.49 mm, 79 faces (baked)
FEATURE [Part::Mirroring] Part__Mirroring001  label="cone-2"
  Base = (0,0,0)
  Normal = (0,1,0)
  Source = -> Loft002
FEATURE [Part::MultiFuse] Fusion  label="two-top-cones"
  Shapes = -> [Loft002,Part__Mirroring001]
FEATURE [App::DocumentObjectGroup] Group006  label="top-cone"
  Group = -> [Loft002,Part__Mirroring001,Fusion]
FEATURE [Part::Feature] Fusion007  label="two-top-cones-1"
  shape: bbox 2.5 x 13.7 x 0.6 mm, 6 faces, 2 solids (baked)
FEATURE [Part::Cut] Cut  label="servo-body-2"
  Base = -> Fillet001007001
  Tool = -> Fusion007
FEATURE [Part::Feature] Pocket002008007005  label="servo-shaft-1"
  Placement = pos=(9.45,0,36) rot=(0,0,1;0rad)
  shape: bbox 14.4 x 14.4 x 5.74 mm, 155 faces (baked)
FEATURE [Part::Feature] Fillet001008001  label="servo-ears-1"
  shape: bbox 55.5 x 18.1 x 4.1 mm, 21 faces (baked)
FEATURE [Part::Feature] Pocket002008007006  label="Servo-wire-holder-1"
  Placement = pos=(20.15,0,2.9) rot=(0,0,1;0rad)
  shape: bbox 1.8 x 6.7 x 4.2 mm, 11 faces (baked)
FEATURE [Part::MultiFuse] Fusion008  label="Servo-no-screws"
  Shapes = -> [Cut,Fillet001008001,Pocket002008007006,Pocket002008007005]
FEATURE [Part::MultiFuse] Fusion009  label="servo-screws"
  Shapes = -> [Fillet001,Fillet001001,Fillet001002,Fillet001003]
FEATURE [App::DocumentObjectGroup] Group004  label="Servo-bottom-screws"
  Group = -> [Revolution,Pocket002006,Fillet,Fillet001,Fillet001001,Fillet001002,Fillet001003,Fusion009]
FEATURE [Part::Feature] Fusion009001  label="servo-screws-four"
  shape: bbox 38.86 x 18.56 x 28.9 mm, 76 faces, 4 solids (baked)
FEATURE [Part::MultiFuse] Fusion009002  label="Servo-Futaba3003-final"
  Shapes = -> [Fusion008,Fusion009001]
FEATURE [Part::MultiFuse] Fusion009003  label="servo-wires"
  Placement = pos=(20,0,2.9) rot=(0,0,1;0rad)
  Shapes = -> [Cylinder,Cylinder002,Cylinder001]
FEATURE [Part::Feature] Fusion009002001  label="Servo-Futaba3003-final001"
  shape: bbox 55.5 x 20 x 41.74 mm, 365 faces (baked)
FEATURE [Part::Feature] Fusion009003001  label="servo-wires001"
  Placement = pos=(20,0,2.9) rot=(0,0,1;0rad)
  shape: bbox 10 x 3.6 x 1.2 mm, 13 faces, 3 solids (baked)
FEATURE [Part::Compound] Compound  label="bottom-Futaba-3003-ready"
  Links = -> [Fusion009002001,Fusion009003001]
  Placement = pos=(31.103,29.7,25.8086) rot=(0,1,0;3.14159rad)
FEATURE [Part::Feature] FTTYB8MHZS8T52Z__1_001001_solid  label="FTTYB8MHZS8T52Z__1_002 (Solid)"
  shape: bbox 104.1 x 59.69 x 69.85 mm, 5828 faces (baked)
FEATURE [Part::Box] Box  label="Cubo"
  Height = 6.35
  Length = 55
  Placement = pos=(-158,79,0) rot=(0,0,1;0rad)
  Width = 20
FEATURE [Part::MultiFuse] Fusion009003002
  Shapes = -> [FTTYB8MHZS8T52Z__1_001001_solid,Box]
FEATURE [App::DocumentObjectGroup] Grupo  label="servo_futaba_components"
  Group = -> [Group,Group001,Group002,Group004,Group005,Group006,Fusion009002,Fusion009003]
FEATURE [Part::Compound] Compound001  label="front-Servo-Futaba-3003"
  Links = -> [Fusion009002001,Fusion009003001]
  Placement = pos=(54.5,29.8,38.4) rot=(0,1,0;1.5708rad)
FEATURE [Part::Box] Box001  label="Cubo001"
  Height = 57
  Length = 6.35
  Placement = pos=(-82.55,69.35,-59.6) rot=(0,0,1;0rad)
  Width = 40
FEATURE [Sketcher::SketchObject] Sketch029  label="futaba_hole001"
  Placement = pos=(95,118.75,168.7) rot=(0.707107,0,0.707107;3.14159rad)
  sketch-geometry (17):
    g0: Circle CenterX=-105.746 CenterY=94.0605 CenterZ=0 NormalX=0 NormalY=0 NormalZ=1 Radius=2.2
    g1: Circle CenterX=-105.746 CenterY=83.9412 CenterZ=0 NormalX=0 NormalY=0 NormalZ=1 Radius=2.2
    g2: Circle CenterX=-154.675 CenterY=83.9412 CenterZ=0 NormalX=0 NormalY=0 NormalZ=1 Radius=2.2
    g3: Circle CenterX=-154.675 CenterY=94.0605 CenterZ=0 NormalX=0 NormalY=0 NormalZ=1 Radius=2.2
    g4: LineSegment StartX=-150.836 StartY=99.4894 StartZ=0 EndX=-109.586 EndY=99.4894 EndZ=0
    g5: LineSegment StartX=-109.586 StartY=78.4894 StartZ=0 EndX=-150.836 EndY=78.4894 EndZ=0
    g6: LineSegment StartX=-150.836 StartY=78.4894 StartZ=0 EndX=-150.836 EndY=99.4894 EndZ=0
    g7: LineSegment StartX=-109.586 StartY=99.4894 StartZ=0 EndX=-109.586 EndY=93 EndZ=0
    g8: LineSegment StartX=-109.586 StartY=93 StartZ=0 EndX=-108 EndY=92 EndZ=0
    g9: LineSegment [constr] StartX=-158.75 StartY=89 StartZ=0 EndX=-108 EndY=89 EndZ=0
    g10: LineSegment StartX=-109.586 StartY=78.4894 StartZ=0 EndX=-109.586 EndY=85 EndZ=0
    g11: LineSegment StartX=-109.586 StartY=85 StartZ=0 EndX=-108 EndY=86 EndZ=0
    g12: LineSegment StartX=-108 StartY=86 StartZ=0 EndX=-108 EndY=87.529 EndZ=0
    g13: LineSegment StartX=-108 StartY=87.529 StartZ=0 EndX=-105.472 EndY=87.529 EndZ=0
    g14: LineSegment StartX=-108 StartY=92 StartZ=0 EndX=-108 EndY=90.4953 EndZ=0
    g15: LineSegment StartX=-108 StartY=90.4953 StartZ=0 EndX=-105.472 EndY=90.4953 EndZ=0
    g16: LineSegment StartX=-105.472 StartY=90.4953 StartZ=0 EndX=-105.472 EndY=87.529 EndZ=0
  constraints (35):
    c: Radius(g0) = 2.2
    c: Equal(g0,g1) = 2.2
    c: DistanceY(g1,g0) = 10.1193
    c: Equal(g0,g3) = 2.2
    c: Equal(g3,g2) = 2.2
    c: DistanceY(g2,g3) = 10.1193
    c: DistanceY(g3,g0) = 0
    c: DistanceX(g2,g3) = 0
    c: DistanceX(g3,g0) = 48.9287
    c: Coincident(g5,g6)
    c: Coincident(g6,g4)
    c: Horizontal(g4)
    c: Horizontal(g5)
    c: Vertical(g6)
    c: DistanceX(g5,g5) = 41.25
    c: DistanceY(g6,g6) = 21
    c: Coincident(g7,g4)
    c: Vertical(g7)
    c: Equal(g4,g5)
    c: Coincident(g7,g8)
    c: Horizontal(g9)
    c: Vertical(g10)
    c: Coincident(g10,g11)
    c: Coincident(g5,g10)
    c: Coincident(g12,g11)
    c: Vertical(g12)
    c: Coincident(g13,g12)
    c: Horizontal(g13)
    c: Coincident(g14,g8)
    c: Vertical(g14)
    c: Coincident(g15,g14)
    c: Horizontal(g15)
    c: Coincident(g16,g15)
    c: Coincident(g16,g13)
    c: Vertical(g16)
FEATURE [PartDesign::Pad] Pad007  label="servo_holes"
  Length = 10
  Length2 = 100
  Placement = pos=(95,118.75,168.7) rot=(0.707107,0,0.707107;3.14159rad)
  Reversed = true
  Sketch = -> Sketch029
  Type = 0
FEATURE [Part::Feature] Part__Feature524  label="Pcb007"
  Placement = pos=(-90.01,145.57,76.85) rot=(0,0,1;0rad)
  shape: bbox 68.58 x 53.34 x 1.6 mm, 170 faces (baked)
FEATURE [Part::Feature] Part__Feature525  label="LED_0603_009"
  Placement = pos=(9.41,44.13,76.85) rot=(0,0,1;0rad)
  shape: bbox 1.65 x 0.725 x 0.675 mm, 50 faces (baked)
FEATURE [Part::Feature] Part__Feature526  label="LED_0603_010"
  Placement = pos=(9.43,48.63,76.85) rot=(0,0,1;0rad)
  shape: bbox 1.65 x 0.725 x 0.675 mm, 50 faces (baked)
FEATURE [Part::Feature] Part__Feature527  label="1x10-socket-header_001"
  Placement = pos=(48.166,54.13,76.85) rot=(0,0,1;0rad)
  shape: bbox 25.4 x 2.54 x 11.85 mm, 186 faces (baked)
FEATURE [Part::Feature] Part__Feature528  label="1x6-male-pin-header-gray_002"
  Placement = pos=(53.5,15.395,76.85) rot=(0,0,1;3.14159rad)
  shape: bbox 15.24 x 2.54 x 11.2 mm, 210 faces (baked)
FEATURE [Part::Feature] Part__Feature529  label="1x8-socket-header_002"
  Placement = pos=(70.01,54.13,76.85) rot=(0,0,1;0rad)
  shape: bbox 20.32 x 2.54 x 11.85 mm, 150 faces (baked)
FEATURE [Part::Feature] Part__Feature530  label="1x8-male-pin-header_001"
  Placement = pos=(70.01,49.685,76.85) rot=(0,0,1;0rad)
  shape: bbox 20.32 x 2.54 x 11.2 mm, 278 faces (baked)
FEATURE [Part::Feature] Part__Feature531  label="1x6-male-pin-header-red_002"
  Placement = pos=(53.5,12.855,76.85) rot=(0,0,1;3.14159rad)
  shape: bbox 15.24 x 2.54 x 11.2 mm, 210 faces (baked)
FEATURE [Part::Feature] Part__Feature532  label="1x8-male-pin-header-red_001"
  Placement = pos=(70.01,47.145,76.85) rot=(0,0,1;0rad)
  shape: bbox 20.32 x 2.54 x 11.2 mm, 278 faces (baked)
FEATURE [Part::Feature] Part__Feature533  label="1x4-male-pin-header-red004_001"
  Placement = pos=(70.7085,27.9426,76.85) rot=(0,0,1;1.5708rad)
  shape: bbox 2.54 x 10.16 x 11.2 mm, 142 faces (baked)
FEATURE [Part::Feature] Part__Feature534  label="1x8-male-pin-header-gray_001"
  Placement = pos=(70.01,44.605,76.85) rot=(0,0,1;0rad)
  shape: bbox 20.32 x 2.54 x 11.2 mm, 278 faces (baked)
FEATURE [Part::Feature] Part__Feature535  label="1x8-socket-header_003"
  Placement = pos=(34.45,5.87,76.85) rot=(0,0,1;3.14159rad)
  shape: bbox 20.32 x 2.54 x 11.85 mm, 150 faces (baked)
FEATURE [Part::Feature] Part__Feature536  label="1x6-socket-header_001"
  Placement = pos=(57.31,5.87,76.85) rot=(0,0,1;3.14159rad)
  shape: bbox 15.24 x 2.54 x 11.85 mm, 114 faces (baked)
FEATURE [Part::Feature] Part__Feature537  label="SOT23-3_003"
  Placement = pos=(16.52,25.43,76.85) rot=(0,0,1;1.5708rad)
  shape: bbox 2.9 x 2.76 x 1.1 mm, 49 faces (baked)
FEATURE [Part::Feature] Part__Feature538  label="1x4-male-pin-header_001"
  Placement = pos=(73.2485,27.9426,76.85) rot=(0,0,1;1.5708rad)
  shape: bbox 2.54 x 10.16 x 11.2 mm, 142 faces (baked)
FEATURE [Part::Feature] Part__Feature539  label="SOT-563_001"
  Placement = pos=(14.0792,32.4384,76.85) rot=(0,0,1;3.14159rad)
  shape: bbox 1.6 x 1.6 x 0.55 mm, 48 faces (baked)
FEATURE [Part::Feature] Part__Feature540  label="1x4-male-pin-header-cyan_001"
  Placement = pos=(68.1685,27.9426,76.85) rot=(0,0,1;1.5708rad)
  shape: bbox 2.54 x 10.16 x 11.2 mm, 142 faces (baked)
FEATURE [Part::Feature] Part__Feature541  label="2x4-pin-header-yello_001"
  Placement = pos=(22.2961,21.1608,76.85) rot=(0,0,1;0rad)
  shape: bbox 10.16 x 5.08 x 11.2 mm, 271 faces (baked)
FEATURE [Part::Feature] Part__Feature542  label="USB-micro-B_001"
  Placement = pos=(8.48,32.25,76.85) rot=(0,0,1;0rad)
  shape: bbox 5.438 x 7.977 x 2.937 mm, 448 faces (baked)
FEATURE [Part::Feature] Part__Feature543  label="slide-sw-right-angle_001"
  Placement = pos=(27.6047,8.537,76.85) rot=(0,0,1;0rad)
  shape: bbox 10 x 7.561 x 5.5 mm, 95 faces (baked)
FEATURE [Part::Feature] Part__Feature544  label="SOT23-3_004"
  Placement = pos=(9.21,21.82,76.85) rot=(0,0,1;0rad)
  shape: bbox 2.76 x 2.9 x 1.1 mm, 49 faces (baked)
FEATURE [Part::Feature] Part__Feature545  label="LED_0603_011"
  Placement = pos=(9.41,45.63,76.85) rot=(0,0,1;0rad)
  shape: bbox 1.65 x 0.725 x 0.675 mm, 50 faces (baked)
FEATURE [Part::Feature] Part__Feature546  label="R_Array_4x0603_002"
  Placement = pos=(13.4696,46.4211,76.85) rot=(0,0,1;3.14159rad)
  shape: bbox 1.62 x 3.498 x 0.5525 mm, 95 faces (baked)
FEATURE [Part::Feature] Part__Feature547  label="LED_0603_012"
  Placement = pos=(9.41,53.13,76.85) rot=(0,0,1;0rad)
  shape: bbox 1.65 x 0.725 x 0.675 mm, 50 faces (baked)
FEATURE [Part::Feature] Part__Feature548  label="sw_smd_6.0x3.8_002"
  Placement = pos=(23.61,47.53,76.85) rot=(0,0,1;0rad)
  shape: bbox 3.899 x 7.3 x 2.5 mm, 90 faces (baked)
FEATURE [Part::Feature] Part__Feature549  label="1x6-pin-header_002"
  Placement = pos=(48.166,49.685,76.85) rot=(0,0,1;0rad)
  shape: bbox 15.24 x 2.54 x 11.2 mm, 210 faces (baked)
FEATURE [Part::Feature] Part__Feature550  label="PVQFN20_002"
  Placement = pos=(62.5043,20.4369,76.85) rot=(0,0,1;3.14159rad)
  shape: bbox 4.52 x 3.52 x 0.9 mm, 133 faces (baked)
FEATURE [Part::Feature] Part__Feature551  label="1x6-pin-header_003"
  Placement = pos=(53.5,10.315,76.85) rot=(0,0,1;3.14159rad)
  shape: bbox 15.24 x 2.54 x 11.2 mm, 210 faces (baked)
FEATURE [Part::Feature] Part__Feature552  label="LED_0603_013"
  Placement = pos=(9.41,54.63,76.85) rot=(0,0,1;0rad)
  shape: bbox 1.65 x 0.725 x 0.675 mm, 50 faces (baked)
FEATURE [Part::Feature] Part__Feature553  label="1x6-male-pin-header-red_003"
  Placement = pos=(48.166,47.145,76.85) rot=(0,0,1;0rad)
  shape: bbox 15.24 x 2.54 x 11.2 mm, 210 faces (baked)
FEATURE [Part::Feature] Part__Feature554  label="LED_0603_014"
  Placement = pos=(9.41,51.63,76.85) rot=(0,0,1;0rad)
  shape: bbox 1.65 x 0.725 x 0.675 mm, 50 faces (baked)
FEATURE [Part::Feature] Part__Feature555  label="1x6-male-pin-header-gray_003"
  Placement = pos=(48.166,44.605,76.85) rot=(0,0,1;0rad)
  shape: bbox 15.24 x 2.54 x 11.2 mm, 210 faces (baked)
FEATURE [Part::Feature] Part__Feature556  label="LED_0603_015"
  Placement = pos=(9.41,47.13,76.85) rot=(0,0,1;0rad)
  shape: bbox 1.65 x 0.725 x 0.675 mm, 50 faces (baked)
FEATURE [Part::Feature] Part__Feature557  label="LED_0603_016"
  Placement = pos=(9.41,50.13,76.85) rot=(0,0,1;0rad)
  shape: bbox 1.65 x 0.725 x 0.675 mm, 50 faces (baked)
FEATURE [Part::Feature] Part__Feature558  label="R_Array_4x0603_003"
  Placement = pos=(13.4696,51.9964,76.85) rot=(0,0,1;3.14159rad)
  shape: bbox 1.62 x 3.498 x 0.5525 mm, 95 faces (baked)
FEATURE [Part::Feature] Part__Feature559  label="LED_0603_017"
  Placement = pos=(33.0022,10.061,76.85) rot=(0,0,1;0rad)
  shape: bbox 1.65 x 0.725 x 0.675 mm, 50 faces (baked)
FEATURE [Part::Feature] Part__Feature560  label="sw_smd_6.0x3.8_003"
  Placement = pos=(18.21,47.53,76.85) rot=(0,0,1;0rad)
  shape: bbox 3.899 x 7.3 x 2.5 mm, 90 faces (baked)
FEATURE [Part::Feature] Part__Feature561  label="PVQFN20_003"
  Placement = pos=(63.0758,38.7122,76.85) rot=(0,0,1;0rad)
  shape: bbox 4.52 x 3.52 x 0.9 mm, 133 faces (baked)
FEATURE [Part::Feature] Part__Feature562  label="SOT23-3_005"
  Placement = pos=(9.21,25.44,76.85) rot=(0,0,1;0rad)
  shape: bbox 2.76 x 2.9 x 1.1 mm, 49 faces (baked)
FEATURE [Part::Feature] Part__Feature563  label="C_0402_053"
  Placement = pos=(33.4467,36.4262,76.85) rot=(0,0,1;1.5708rad)
  shape: bbox 0.5 x 0.985 x 0.5 mm, 44 faces (baked)
FEATURE [Part::Feature] Part__Feature564  label="MSOP-8_001"
  Placement = pos=(22.9438,39.7917,76.85) rot=(0,0,1;0rad)
  shape: bbox 5.141 x 3.2 x 1 mm, 115 faces (baked)
FEATURE [Part::Feature] Part__Feature565  label="xtal-3_2x2_5_001"
  Placement = pos=(16.2509,38.8265,76.85) rot=(0,0,1;0rad)
  shape: bbox 2.5 x 3.2 x 0.92 mm, 29 faces (baked)
FEATURE [Part::Feature] Part__Feature566  label="F1812-505k_001"
  Placement = pos=(10.28,41.09,76.85) rot=(0,0,1;3.14159rad)
  shape: bbox 4.73 x 3.41 x 1.39 mm, 94 faces (baked)
FEATURE [Part::Feature] Part__Feature567  label="jack_DC_2.1mm_PCB_001"
  Placement = pos=(11.9202,11.6866,76.85) rot=(0,0,-1;1.5708rad)
  shape: bbox 14.5 x 9.46 x 14.8 mm, 34 faces (baked)
FEATURE [Part::Feature] Part__Feature568  label="DO-214AC_001"
  Placement = pos=(10.7772,18.2398,76.85) rot=(0,0,1;3.14159rad)
  shape: bbox 5.475 x 2.8 x 2.574 mm, 39 faces (baked)
FEATURE [Part::Feature] Part__Feature569  label="SOD-323_002"
  Placement = pos=(13.3426,26.8504,76.85) rot=(0,0,1;0rad)
  shape: bbox 2.6 x 1.35 x 1.113 mm, 38 faces (baked)
FEATURE [Part::Feature] Part__Feature570  label="DFN-2523-6_003"
  Placement = pos=(20.6832,18.2652,76.85) rot=(0,0,-1;1.5708rad)
  shape: bbox 2.4 x 2.5 x 0.62 mm, 44 faces (baked)
FEATURE [Part::Feature] Part__Feature571  label="DFN-2523-6_004"
  Placement = pos=(16.3398,18.2271,76.85) rot=(0,0,1;1.5708rad)
  shape: bbox 2.4 x 2.5 x 0.62 mm, 44 faces (baked)
FEATURE [Part::Feature] Part__Feature572  label="C_0402_054"
  Placement = pos=(27.6047,46.8275,76.85) rot=(0,0,-1;1.5708rad)
  shape: bbox 0.5 x 0.985 x 0.5 mm, 44 faces (baked)
FEATURE [Part::Feature] Part__Feature573  label="DFN-2523-6_005"
  Placement = pos=(40.9016,9.934,76.85) rot=(0,0,-1;1.5708rad)
  shape: bbox 2.4 x 2.5 x 0.62 mm, 44 faces (baked)
FEATURE [Part::Feature] Part__Feature574  label="PVQFN16_001"
  Placement = pos=(31.28,45.82,76.85) rot=(0,0,1;0rad)
  shape: bbox 4.17 x 3.7 x 1.1 mm, 109 faces (baked)
FEATURE [Part::Feature] Part__Feature575  label="C_0402_055"
  Placement = pos=(66.1111,21.2243,76.85) rot=(0,0,1;1.5708rad)
  shape: bbox 0.5 x 0.985 x 0.5 mm, 44 faces (baked)
FEATURE [Part::Feature] Part__Feature576  label="L_4040_001"
  Placement = pos=(32.7609,14.9505,76.85) rot=(0,0,-1;1.5708rad)
  shape: bbox 4.3 x 4.3 x 2.33 mm, 122 faces (baked)
FEATURE [Part::Feature] Part__Feature577  label="QFN16_002"
  Placement = pos=(62.7837,29.5174,76.85) rot=(0,0,1;0rad)
  shape: bbox 3.08 x 3.08 x 0.9 mm, 118 faces (baked)
FEATURE [Part::Feature] Part__Feature578  label="QFN16_003"
  Placement = pos=(27.9222,15.3569,76.85) rot=(0,0,1;3.14159rad)
  shape: bbox 3.08 x 3.08 x 0.9 mm, 118 faces (baked)
FEATURE [Part::Feature] Part__Feature579  label="C_0402_056"
  Placement = pos=(12.1996,38.2042,76.85) rot=(0,0,1;3.14159rad)
  shape: bbox 0.985 x 0.5 x 0.5 mm, 44 faces (baked)
FEATURE [Part::Feature] Part__Feature580  label="FTDI-QFN-64_001"
  Placement = pos=(23.0581,31.4732,76.85) rot=(0,0,1;0rad)
  shape: bbox 9.04 x 9.04 x 0.95 mm, 849 faces (baked)
FEATURE [Part::Feature] Part__Feature581  label="C_0402_057"
  Placement = pos=(30.3098,50.3327,76.85) rot=(0,0,1;1.5708rad)
  shape: bbox 0.5 x 0.985 x 0.5 mm, 44 faces (baked)
FEATURE [Part::Feature] Part__Feature582  label="C_0402_058"
  Placement = pos=(16.8097,29.7333,76.85) rot=(0,0,1;3.14159rad)
  shape: bbox 0.985 x 0.5 x 0.5 mm, 44 faces (baked)
FEATURE [Part::Feature] Part__Feature583  label="C_0402_059"
  Placement = pos=(59.6087,39.8298,76.85) rot=(0,0,-1;1.5708rad)
  shape: bbox 0.5 x 0.985 x 0.5 mm, 44 faces (baked)
FEATURE [Part::Feature] Part__Feature584  label="C_1206_002"
  Placement = pos=(28.1762,10.9627,76.85) rot=(0,0,1;3.14159rad)
  shape: bbox 3.2 x 1.6 x 1 mm, 44 faces (baked)
FEATURE [Part::Feature] Part__Feature585  label="C_0402_060"
  Placement = pos=(29.2938,12.601,76.85) rot=(0,0,1;3.14159rad)
  shape: bbox 0.985 x 0.5 x 0.5 mm, 44 faces (baked)
FEATURE [Part::Feature] Part__Feature586  label="C_0402_061"
  Placement = pos=(33.3197,50.3327,76.85) rot=(0,0,1;1.5708rad)
  shape: bbox 0.5 x 0.985 x 0.5 mm, 44 faces (baked)
FEATURE [Part::Feature] Part__Feature587  label="C_0402_062"
  Placement = pos=(33.0022,25.7201,76.85) rot=(0,0,1;3.14159rad)
  shape: bbox 0.985 x 0.5 x 0.5 mm, 44 faces (baked)
FEATURE [Part::Feature] Part__Feature588  label="C_0603_014"
  Placement = pos=(26.8046,18.6335,76.85) rot=(0,0,1;0rad)
  shape: bbox 1.6 x 0.8 x 0.6 mm, 44 faces (baked)
FEATURE [Part::Feature] Part__Feature589  label="C_0402_063"
  Placement = pos=(26.6141,46.8275,76.85) rot=(0,0,1;1.5708rad)
  shape: bbox 0.5 x 0.985 x 0.5 mm, 44 faces (baked)
FEATURE [Part::Feature] Part__Feature590  label="C_0402_064"
  Placement = pos=(31.31,50.33,76.85) rot=(0,0,1;1.5708rad)
  shape: bbox 0.5 x 0.985 x 0.5 mm, 44 faces (baked)
FEATURE [Part::Feature] Part__Feature591  label="DFN-3030-8_001"
  Placement = pos=(37.3202,16.1062,76.85) rot=(0,0,1;3.14159rad)
  shape: bbox 3.02 x 3 x 0.85 mm, 89 faces (baked)
FEATURE [Part::Feature] Part__Feature592  label="C_0603_015"
  Placement = pos=(29.6113,18.3287,76.85) rot=(0,0,1;0rad)
  shape: bbox 1.6 x 0.8 x 0.6 mm, 44 faces (baked)
FEATURE [Part::Feature] Part__Feature593  label="C_0402_065"
  Placement = pos=(16.8097,30.635,76.85) rot=(0,0,1;0rad)
  shape: bbox 0.985 x 0.5 x 0.5 mm, 44 faces (baked)
FEATURE [Part::Feature] Part__Feature594  label="C_0402_066"
  Placement = pos=(47.6707,17.5159,76.85) rot=(0,0,1;0rad)
  shape: bbox 0.985 x 0.5 x 0.5 mm, 44 faces (baked)
FEATURE [Part::Feature] Part__Feature595  label="C_0402_067"
  Placement = pos=(43.7083,17.5286,76.85) rot=(0,0,1;3.14159rad)
  shape: bbox 0.985 x 0.5 x 0.5 mm, 44 faces (baked)
FEATURE [Part::Feature] Part__Feature596  label="C_0402_068"
  Placement = pos=(20.353,25.7582,76.85) rot=(0,0,1;3.14159rad)
  shape: bbox 0.985 x 0.5 x 0.5 mm, 44 faces (baked)
FEATURE [Part::Feature] Part__Feature597  label="C_0402_069"
  Placement = pos=(22.8549,37.1755,76.85) rot=(0,0,1;3.14159rad)
  shape: bbox 0.985 x 0.5 x 0.5 mm, 44 faces (baked)
FEATURE [Part::Feature] Part__Feature598  label="C_0402_070"
  Placement = pos=(58.199,28.5268,76.85) rot=(0,0,-1;1.5708rad)
  shape: bbox 0.5 x 0.985 x 0.5 mm, 44 faces (baked)
FEATURE [Part::Feature] Part__Feature599  label="C_0603_016"
  Placement = pos=(32.5069,21.6307,76.85) rot=(0,0,1;1.5708rad)
  shape: bbox 0.8 x 1.6 x 0.6 mm, 44 faces (baked)
FEATURE [Part::Feature] Part__Feature600  label="C_0402_071"
  Placement = pos=(63.7108,42.3317,76.85) rot=(0,0,1;0rad)
  shape: bbox 0.985 x 0.5 x 0.5 mm, 44 faces (baked)
FEATURE [Part::Feature] Part__Feature601  label="C_0603_017"
  Placement = pos=(16.5938,35.7404,76.85) rot=(0,0,1;3.14159rad)
  shape: bbox 1.6 x 0.8 x 0.6 mm, 44 faces (baked)
FEATURE [Part::Feature] Part__Feature602  label="pushbutton-right-angle_001"
  Placement = pos=(72.169,20.221,76.85) rot=(0,0,1;1.5708rad)
  shape: bbox 7.9 x 7.4 x 11 mm, 130 faces (baked)
FEATURE [Part::Feature] Part__Feature603  label="C_0402_072"
  Placement = pos=(27.6047,44.1351,76.85) rot=(0,0,-1;1.5708rad)
  shape: bbox 0.5 x 0.985 x 0.5 mm, 44 faces (baked)
FEATURE [Part::Feature] Part__Feature604  label="C_0402_073"
  Placement = pos=(27.1729,25.7328,76.85) rot=(0,0,1;0rad)
  shape: bbox 0.985 x 0.5 x 0.5 mm, 44 faces (baked)
FEATURE [Part::Feature] Part__Feature605  label="C_0402_074"
  Placement = pos=(59.6087,37.62,76.85) rot=(0,0,-1;1.5708rad)
  shape: bbox 0.5 x 0.985 x 0.5 mm, 44 faces (baked)
FEATURE [Part::Feature] Part__Feature606  label="WSON-6_001"
  Placement = pos=(38.2854,12.728,76.85) rot=(0,0,1;0rad)
  shape: bbox 1.6 x 1.55 x 0.85 mm, 44 faces (baked)
FEATURE [Part::Feature] Part__Feature607  label="C_0402_075"
  Placement = pos=(56.8782,19.2304,76.85) rot=(0,0,-1;1.5708rad)
  shape: bbox 0.5 x 0.985 x 0.5 mm, 44 faces (baked)
FEATURE [Part::Feature] Part__Feature608  label="TQFP-144_001"
  Placement = pos=(45.9308,30,76.85) rot=(0,0,1;0rad)
  shape: bbox 21.98 x 21.98 x 1.12 mm, 2168 faces (baked)
FEATURE [Part::Feature] Part__Feature609  label="C_0603_018"
  Placement = pos=(40.1142,12.9058,76.85) rot=(0,0,-1;1.5708rad)
  shape: bbox 0.8 x 1.6 x 0.6 mm, 44 faces (baked)
FEATURE [Part::Feature] Part__Feature610  label="C_0402_076"
  Placement = pos=(19.1084,39.9314,76.85) rot=(0,0,1;1.5708rad)
  shape: bbox 0.5 x 0.985 x 0.5 mm, 44 faces (baked)
FEATURE [Part::Feature] Part__Feature611  label="C_0603_019"
  Placement = pos=(21.8008,14.9378,76.85) rot=(0,0,-1;1.5708rad)
  shape: bbox 0.8 x 1.6 x 0.6 mm, 44 faces (baked)
FEATURE [Part::Feature] Part__Feature612  label="C_0402_077"
  Placement = pos=(66.2,42.319,76.85) rot=(0,0,1;3.14159rad)
  shape: bbox 0.985 x 0.5 x 0.5 mm, 44 faces (baked)
FEATURE [Part::Feature] Part__Feature613  label="C_0402_078"
  Placement = pos=(68.7146,42.3317,76.85) rot=(0,0,1;0rad)
  shape: bbox 0.985 x 0.5 x 0.5 mm, 44 faces (baked)
FEATURE [Part::Feature] Part__Feature614  label="C_0402_079"
  Placement = pos=(28.3032,50.3327,76.85) rot=(0,0,1;1.5708rad)
  shape: bbox 0.5 x 0.985 x 0.5 mm, 44 faces (baked)
FEATURE [Part::Feature] Part__Feature615  label="L_0603_003"
  Placement = pos=(12.5044,36.0325,76.85) rot=(0,0,1;1.5708rad)
  shape: bbox 0.8 x 1.6 x 0.6 mm, 44 faces (baked)
FEATURE [Part::Feature] Part__Feature616  label="C_0402_080"
  Placement = pos=(26.0934,37.1374,76.85) rot=(0,0,1;3.14159rad)
  shape: bbox 0.985 x 0.5 x 0.5 mm, 44 faces (baked)
FEATURE [Part::Feature] Part__Feature617  label="C_0603_020"
  Placement = pos=(10.0533,38.2042,76.85) rot=(0,0,1;0rad)
  shape: bbox 1.6 x 0.8 x 0.6 mm, 44 faces (baked)
FEATURE [Part::Feature] Part__Feature618  label="C_0402_081"
  Placement = pos=(58.199,35.4229,76.85) rot=(0,0,1;1.5708rad)
  shape: bbox 0.5 x 0.985 x 0.5 mm, 44 faces (baked)
FEATURE [Part::Feature] Part__Feature619  label="R_0402_037"
  Placement = pos=(16.797,33.6322,76.85) rot=(0,0,1;0rad)
  shape: bbox 1 x 0.5 x 0.3 mm, 40 faces (baked)
FEATURE [Part::Feature] Part__Feature620  label="C_0402_082"
  Placement = pos=(29.2049,32.2352,76.85) rot=(0,0,1;0rad)
  shape: bbox 0.985 x 0.5 x 0.5 mm, 44 faces (baked)
FEATURE [Part::Feature] Part__Feature621  label="C_0402_083"
  Placement = pos=(32.3037,50.3327,76.85) rot=(0,0,1;1.5708rad)
  shape: bbox 0.5 x 0.985 x 0.5 mm, 44 faces (baked)
FEATURE [Part::Feature] Part__Feature622  label="C_0603_021"
  Placement = pos=(66.0095,33.429,76.85) rot=(0,0,1;1.5708rad)
  shape: bbox 0.8 x 1.6 x 0.6 mm, 44 faces (baked)
FEATURE [Part::Feature] Part__Feature623  label="C_1206_003"
  Placement = pos=(23.8963,13.49,76.85) rot=(0,0,-1;1.5708rad)
  shape: bbox 1.6 x 3.2 x 1 mm, 44 faces (baked)
FEATURE [Part::Feature] Part__Feature624  label="C_0603_022"
  Placement = pos=(14.2316,30.3429,76.85) rot=(0,0,1;3.14159rad)
  shape: bbox 1.6 x 0.8 x 0.6 mm, 44 faces (baked)
FEATURE [Part::Feature] Part__Feature625  label="C_0402_084"
  Placement = pos=(19.21,37.2898,76.85) rot=(0,0,1;3.14159rad)
  shape: bbox 0.985 x 0.5 x 0.5 mm, 44 faces (baked)
FEATURE [Part::Feature] Part__Feature626  label="C_0603_023"
  Placement = pos=(12.6568,20.729,76.85) rot=(0,0,1;0rad)
  shape: bbox 1.6 x 0.8 x 0.6 mm, 44 faces (baked)
FEATURE [Part::Feature] Part__Feature627  label="C_0402_085"
  Placement = pos=(26.61,44.13,76.85) rot=(0,0,-1;1.5708rad)
  shape: bbox 0.5 x 0.985 x 0.5 mm, 44 faces (baked)
FEATURE [Part::Feature] Part__Feature628  label="SOD-323_003"
  Placement = pos=(58.32,38.1,76.85) rot=(0,0,-1;1.5708rad)
  shape: bbox 1.35 x 2.6 x 1.113 mm, 38 faces (baked)
FEATURE [Part::Feature] Part__Feature629  label="DFN-8-6x5mm_001"
  Placement = pos=(47.61,13.9,76.85) rot=(0,0,1;3.14159rad)
  shape: bbox 6.1 x 5 x 0.9466 mm, 62 faces (baked)
FEATURE [Part::Feature] Part__Feature630  label="C_0402_086"
  Placement = pos=(28.8112,29.1364,76.85) rot=(0,0,-1;1.5708rad)
  shape: bbox 0.5 x 0.985 x 0.5 mm, 44 faces (baked)
FEATURE [Part::Feature] Part__Feature631  label="L_0603_004"
  Placement = pos=(14.4856,35.1054,76.85) rot=(0,0,1;1.5708rad)
  shape: bbox 0.8 x 1.6 x 0.6 mm, 44 faces (baked)
FEATURE [Part::Feature] Part__Feature632  label="C_0402_087"
  Placement = pos=(58.2117,31.524,76.85) rot=(0,0,1;1.5708rad)
  shape: bbox 0.5 x 0.985 x 0.5 mm, 44 faces (baked)
FEATURE [Part::Feature] Part__Feature633  label="C_0603_024"
  Placement = pos=(19.0068,22.5832,76.85) rot=(0,0,-1;1.5708rad)
  shape: bbox 0.8 x 1.6 x 0.6 mm, 44 faces (baked)
FEATURE [Part::Feature] Part__Feature634  label="C_0603_025"
  Placement = pos=(39.9999,16.6523,76.85) rot=(0,0,1;1.5708rad)
  shape: bbox 0.8 x 1.6 x 0.6 mm, 44 faces (baked)
FEATURE [Part::Feature] Part__Feature635  label="R_0402_038"
  Placement = pos=(29.8145,40.5283,76.85) rot=(0,0,1;1.5708rad)
  shape: bbox 0.5 x 1 x 0.3 mm, 40 faces (baked)
FEATURE [Part::Feature] Part__Feature636  label="C_0402_088"
  Placement = pos=(61.1073,42.3317,76.85) rot=(0,0,1;3.14159rad)
  shape: bbox 0.985 x 0.5 x 0.5 mm, 44 faces (baked)
FEATURE [Part::Feature] Part__Feature637  label="C_0402_089"
  Placement = pos=(33.0022,24.2342,76.85) rot=(0,0,1;3.14159rad)
  shape: bbox 0.985 x 0.5 x 0.5 mm, 44 faces (baked)
FEATURE [Part::Feature] Part__Feature638  label="C_0402_090"
  Placement = pos=(33.6118,21.4275,76.85) rot=(0,0,1;1.5708rad)
  shape: bbox 0.5 x 0.985 x 0.5 mm, 44 faces (baked)
FEATURE [Part::Feature] Part__Feature639  label="L_0603_005"
  Placement = pos=(23.909,16.9317,76.85) rot=(0,0,1;0rad)
  shape: bbox 1.6 x 0.8 x 0.6 mm, 44 faces (baked)
FEATURE [Part::Feature] Part__Feature640  label="C_0603_026"
  Placement = pos=(28.735,35.3721,76.85) rot=(0,0,-1;1.5708rad)
  shape: bbox 0.8 x 1.6 x 0.6 mm, 44 faces (baked)
FEATURE [Part::Feature] Part__Feature641  label="C_0402_091"
  Placement = pos=(66.1111,19.332,76.85) rot=(0,0,1;1.5708rad)
  shape: bbox 0.5 x 0.985 x 0.5 mm, 44 faces (baked)
FEATURE [Part::Feature] Part__Feature642  label="L_0805_001"
  Placement = pos=(13.6728,28.8824,76.85) rot=(0,0,1;0rad)
  shape: bbox 2 x 1.25 x 1.25 mm, 50 faces (baked)
FEATURE [Part::Feature] Part__Feature643  label="C_0402_092"
  Placement = pos=(29.3065,50.3327,76.85) rot=(0,0,1;1.5708rad)
  shape: bbox 0.5 x 0.985 x 0.5 mm, 44 faces (baked)
FEATURE [Part::Feature] Part__Feature644  label="C_0402_093"
  Placement = pos=(16.797,34.6228,76.85) rot=(0,0,1;3.14159rad)
  shape: bbox 0.985 x 0.5 x 0.5 mm, 44 faces (baked)
FEATURE [Part::Feature] Part__Feature645  label="R_0402_039"
  Placement = pos=(26.8046,40.5283,76.85) rot=(0,0,1;1.5708rad)
  shape: bbox 0.5 x 1 x 0.3 mm, 40 faces (baked)
FEATURE [Part::Feature] Part__Feature646  label="C_0402_094"
  Placement = pos=(71.3054,42.3317,76.85) rot=(0,0,1;3.14159rad)
  shape: bbox 0.985 x 0.5 x 0.5 mm, 44 faces (baked)
FEATURE [Part::Feature] Part__Feature647  label="C_0402_095"
  Placement = pos=(16.7081,41.3665,76.85) rot=(0,0,1;3.14159rad)
  shape: bbox 0.985 x 0.5 x 0.5 mm, 44 faces (baked)
FEATURE [Part::Feature] Part__Feature648  label="C_0402_096"
  Placement = pos=(42.9082,12.5375,76.85) rot=(0,0,1;1.5708rad)
  shape: bbox 0.5 x 0.985 x 0.5 mm, 44 faces (baked)
FEATURE [Part::Feature] Part__Feature649  label="C_0402_097"
  Placement = pos=(41.7652,17.1349,76.85) rot=(0,0,-1;1.5708rad)
  shape: bbox 0.5 x 0.985 x 0.5 mm, 44 faces (baked)
FEATURE [Part::Feature] Part__Feature650  label="C_0402_098"
  Placement = pos=(63.5076,32.3368,76.85) rot=(0,0,1;3.14159rad)
  shape: bbox 0.985 x 0.5 x 0.5 mm, 44 faces (baked)
FEATURE [Part::Feature] Part__Feature651  label="C_0402_099"
  Placement = pos=(61.6153,32.3368,76.85) rot=(0,0,1;3.14159rad)
  shape: bbox 0.985 x 0.5 x 0.5 mm, 44 faces (baked)
FEATURE [Part::Feature] Part__Feature652  label="C_0603_027"
  Placement = pos=(41.3207,12.9058,76.85) rot=(0,0,-1;1.5708rad)
  shape: bbox 0.8 x 1.6 x 0.6 mm, 44 faces (baked)
FEATURE [Part::Feature] Part__Feature653  label="C_0402_100"
  Placement = pos=(58.6054,42.3317,76.85) rot=(0,0,1;0rad)
  shape: bbox 0.985 x 0.5 x 0.5 mm, 44 faces (baked)
FEATURE [Part::Feature] Part__Feature654  label="C_0402_101"
  Placement = pos=(56.0019,42.3317,76.85) rot=(0,0,1;0rad)
  shape: bbox 0.985 x 0.5 x 0.5 mm, 44 faces (baked)
FEATURE [Part::Feature] Part__Feature655  label="C_0402_102"
  Placement = pos=(53.4111,42.3317,76.85) rot=(0,0,1;3.14159rad)
  shape: bbox 0.985 x 0.5 x 0.5 mm, 44 faces (baked)
FEATURE [Part::Feature] Part__Feature656  label="C_0402_103"
  Placement = pos=(47.0738,42.3317,76.85) rot=(0,0,1;3.14159rad)
  shape: bbox 0.985 x 0.5 x 0.5 mm, 44 faces (baked)
FEATURE [Part::Feature] Part__Feature657  label="C_0402_104"
  Placement = pos=(50.706,42.3317,76.85) rot=(0,0,1;3.14159rad)
  shape: bbox 0.985 x 0.5 x 0.5 mm, 44 faces (baked)
FEATURE [Part::Feature] Part__Feature658  label="C_0402_105"
  Placement = pos=(42.0319,42.4333,76.85) rot=(0,0,1;0rad)
  shape: bbox 0.985 x 0.5 x 0.5 mm, 44 faces (baked)
FEATURE [Part::Feature] Part__Feature659  label="R_0402_040"
  Placement = pos=(28.8112,40.5283,76.85) rot=(0,0,-1;1.5708rad)
  shape: bbox 0.5 x 1 x 0.3 mm, 40 faces (baked)
FEATURE [Part::Feature] Part__Feature660  label="R_0402_041"
  Placement = pos=(27.8079,40.5283,76.85) rot=(0,0,-1;1.5708rad)
  shape: bbox 0.5 x 1 x 0.3 mm, 40 faces (baked)
FEATURE [Part::Feature] Part__Feature661  label="R_0402_042"
  Placement = pos=(16.81,28.33,76.85) rot=(0,0,1;0rad)
  shape: bbox 1 x 0.5 x 0.3 mm, 40 faces (baked)
FEATURE [Part::Feature] Part__Feature662  label="R_0402_043"
  Placement = pos=(14.2062,25.0343,76.85) rot=(0,0,1;1.5708rad)
  shape: bbox 0.5 x 1 x 0.3 mm, 40 faces (baked)
FEATURE [Part::Feature] Part__Feature663  label="R_0402_044"
  Placement = pos=(12.5044,25.5296,76.85) rot=(0,0,1;3.14159rad)
  shape: bbox 1 x 0.5 x 0.3 mm, 40 faces (baked)
FEATURE [Part::Feature] Part__Feature664  label="R_0402_045"
  Placement = pos=(12.5044,24.539,76.85) rot=(0,0,1;3.14159rad)
  shape: bbox 1 x 0.5 x 0.3 mm, 40 faces (baked)
FEATURE [Part::Feature] Part__Feature665  label="R_0402_046"
  Placement = pos=(16.9113,22.3292,76.85) rot=(0,0,1;3.14159rad)
  shape: bbox 1 x 0.5 x 0.3 mm, 40 faces (baked)
FEATURE [Part::Feature] Part__Feature666  label="R_0402_047"
  Placement = pos=(14.9047,20.729,76.85) rot=(0,0,1;3.14159rad)
  shape: bbox 1 x 0.5 x 0.3 mm, 40 faces (baked)
FEATURE [Part::Feature] Part__Feature667  label="R_0402_048"
  Placement = pos=(15.0063,22.3292,76.85) rot=(0,0,1;3.14159rad)
  shape: bbox 1 x 0.5 x 0.3 mm, 40 faces (baked)
FEATURE [Part::Feature] Part__Feature668  label="R_0402_049"
  Placement = pos=(16.797,20.729,76.85) rot=(0,0,1;0rad)
  shape: bbox 1 x 0.5 x 0.3 mm, 40 faces (baked)
FEATURE [Part::Feature] Part__Feature669  label="R_0402_050"
  Placement = pos=(33.8023,8.4227,76.85) rot=(0,0,1;1.5708rad)
  shape: bbox 0.5 x 1 x 0.3 mm, 40 faces (baked)
FEATURE [Part::Feature] Part__Feature670  label="R_0402_051"
  Placement = pos=(18.702,20.729,76.85) rot=(0,0,1;0rad)
  shape: bbox 1 x 0.5 x 0.3 mm, 40 faces (baked)
FEATURE [Part::Feature] Part__Feature671  label="R_0402_052"
  Placement = pos=(33.0022,19.7257,76.85) rot=(0,0,1;3.14159rad)
  shape: bbox 1 x 0.5 x 0.3 mm, 40 faces (baked)
FEATURE [Part::Feature] Part__Feature672  label="R_0402_053"
  Placement = pos=(33.0022,28.73,76.85) rot=(0,0,1;0rad)
  shape: bbox 1 x 0.5 x 0.3 mm, 40 faces (baked)
FEATURE [Part::Feature] Part__Feature673  label="R_0402_054"
  Placement = pos=(36.3042,12.728,76.85) rot=(0,0,-1;1.5708rad)
  shape: bbox 0.5 x 1 x 0.3 mm, 40 faces (baked)
FEATURE [Part::Feature] Part__Feature674  label="R_0402_055"
  Placement = pos=(50.706,17.5286,76.85) rot=(0,0,1;3.14159rad)
  shape: bbox 1 x 0.5 x 0.3 mm, 40 faces (baked)
FEATURE [Part::Feature] Part__Feature675  label="R_0402_056"
  Placement = pos=(36.7106,11.0262,76.85) rot=(0,0,1;3.14159rad)
  shape: bbox 1 x 0.5 x 0.3 mm, 40 faces (baked)
FEATURE [Part::Feature] Part__Feature676  label="R_0402_057"
  Placement = pos=(58.707,23.1293,76.85) rot=(0,0,1;0rad)
  shape: bbox 1 x 0.5 x 0.3 mm, 40 faces (baked)
FEATURE [Part::Feature] Part__Feature677  label="R_0402_058"
  Placement = pos=(36.7106,10.0356,76.85) rot=(0,0,1;3.14159rad)
  shape: bbox 1 x 0.5 x 0.3 mm, 40 faces (baked)
FEATURE [Part::Feature] Part__Feature678  label="R_0402_059"
  Placement = pos=(47.2135,9.9213,76.85) rot=(0,0,1;1.5708rad)
  shape: bbox 0.5 x 1 x 0.3 mm, 40 faces (baked)
FEATURE [Part::Feature] Part__Feature679  label="R_0402_060"
  Placement = pos=(46.2102,9.9213,76.85) rot=(0,0,1;1.5708rad)
  shape: bbox 0.5 x 1 x 0.3 mm, 40 faces (baked)
FEATURE [Part::Feature] Part__Feature680  label="R_0402_061"
  Placement = pos=(48.2041,9.9213,76.85) rot=(0,0,1;1.5708rad)
  shape: bbox 0.5 x 1 x 0.3 mm, 40 faces (baked)
FEATURE [Part::Feature] Part__Feature681  label="R_0402_062"
  Placement = pos=(68.2066,12.2327,76.85) rot=(0,0,-1;1.5708rad)
  shape: bbox 0.5 x 1 x 0.3 mm, 40 faces (baked)
FEATURE [Part::Feature] Part__Feature682  label="R_0402_063"
  Placement = pos=(49.2074,9.9213,76.85) rot=(0,0,1;1.5708rad)
  shape: bbox 0.5 x 1 x 0.3 mm, 40 faces (baked)
FEATURE [Part::Feature] Part__Feature683  label="R_0402_064"
  Placement = pos=(68.2066,10.1245,76.85) rot=(0,0,1;1.5708rad)
  shape: bbox 0.5 x 1 x 0.3 mm, 40 faces (baked)
FEATURE [Part::Feature] Part__Feature684  label="R_0402_065"
  Placement = pos=(67.3049,21.2243,76.85) rot=(0,0,1;1.5708rad)
  shape: bbox 0.5 x 1 x 0.3 mm, 40 faces (baked)
FEATURE [Part::Feature] Part__Feature685  label="R_0402_066"
  Placement = pos=(59.9008,28.1331,76.85) rot=(0,0,-1;1.5708rad)
  shape: bbox 0.5 x 1 x 0.3 mm, 40 faces (baked)
FEATURE [Part::Feature] Part__Feature686  label="R_0402_067"
  Placement = pos=(67.3049,19.332,76.85) rot=(0,0,-1;1.5708rad)
  shape: bbox 0.5 x 1 x 0.3 mm, 40 faces (baked)
FEATURE [Part::Feature] Part__Feature687  label="R_0402_068"
  Placement = pos=(66,35.63,76.85) rot=(0,0,1;1.5708rad)
  shape: bbox 0.5 x 1 x 0.3 mm, 40 faces (baked)
FEATURE [Part::Feature] Part__Feature688  label="R_0402_069"
  Placement = pos=(59.9008,31.1303,76.85) rot=(0,0,1;1.5708rad)
  shape: bbox 0.5 x 1 x 0.3 mm, 40 faces (baked)
FEATURE [Part::Feature] Part__Feature689  label="R_0402_070"
  Placement = pos=(12.5044,23.523,76.85) rot=(0,0,1;0rad)
  shape: bbox 1 x 0.5 x 0.3 mm, 40 faces (baked)
FEATURE [Part::Feature] Part__Feature690  label="R_0402_071"
  Placement = pos=(12.5044,22.3292,76.85) rot=(0,0,1;3.14159rad)
  shape: bbox 1 x 0.5 x 0.3 mm, 40 faces (baked)
FEATURE [Part::Feature] Part__Feature691  label="R_0402_072"
  Placement = pos=(23.2105,25.7328,76.85) rot=(0,0,1;3.14159rad)
  shape: bbox 1 x 0.5 x 0.3 mm, 40 faces (baked)
FEATURE [Part::Feature] Part__Feature692  label="R_0402_073"
  Placement = pos=(25.1028,25.7328,76.85) rot=(0,0,1;0rad)
  shape: bbox 1 x 0.5 x 0.3 mm, 40 faces (baked)
FEATURE [Part::Feature] Part__Feature693  label="1x3-pin-header_001"
  Placement = pos=(68.0796,37.6581,76.85) rot=(0,0,-1;1.5708rad)
  shape: bbox 2.54 x 7.62 x 11.2 mm, 108 faces (baked)
FEATURE [Part::Feature] Part__Feature694  label="jumper-cap-2.54mm_001"
  Placement = pos=(68.0796,37.6581,76.85) rot=(0,0,1;1.5708rad)
  shape: bbox 2.5 x 5 x 6 mm, 108 faces (baked)
FEATURE [App::DocumentObjectGroup] Grupo028  label="step001"
  Group = -> [Part__Feature524,Part__Feature525,Part__Feature526,Part__Feature527,Part__Feature528,Part__Feature529,Part__Feature530,Part__Feature531,Part__Feature532,Part__Feature533,Part__Feature534,Part__Feature535,Part__Feature536,Part__Feature537,Part__Feature538,Part__Feature539,Part__Feature540,Part__Feature541,Part__Feature542,Part__Feature543,Part__Feature544,Part__Feature545,Part__Feature546,+148 more]
FEATURE [App::DocumentObjectGroup] Grupo027  label="icezum_alhambra001"
  Group = -> [Grupo028]
FEATURE [Sketcher::SketchObject] Sketch030  label="futaba_hole002"
  Placement = pos=(-260.45,178,-2) rot=(0,0,1;3.14159rad)
  sketch-geometry (14):
    g0: Circle CenterX=-105.746 CenterY=94.0605 CenterZ=0 NormalX=0 NormalY=0 NormalZ=1 Radius=2.2
    g1: Circle CenterX=-105.746 CenterY=83.9412 CenterZ=0 NormalX=0 NormalY=0 NormalZ=1 Radius=2.2
    g2: Circle CenterX=-154.675 CenterY=83.9412 CenterZ=0 NormalX=0 NormalY=0 NormalZ=1 Radius=2.2
    g3: Circle CenterX=-154.675 CenterY=94.0605 CenterZ=0 NormalX=0 NormalY=0 NormalZ=1 Radius=2.2
    g4: LineSegment StartX=-150.836 StartY=99.4894 StartZ=0 EndX=-109.586 EndY=99.4894 EndZ=0
    g5: LineSegment StartX=-109.586 StartY=78.4894 StartZ=0 EndX=-150.836 EndY=78.4894 EndZ=0
    g6: LineSegment StartX=-150.836 StartY=78.4894 StartZ=0 EndX=-150.836 EndY=99.4894 EndZ=0
    g7: LineSegment StartX=-109.586 StartY=99.4894 StartZ=0 EndX=-109.586 EndY=93 EndZ=0
    g8: LineSegment StartX=-109.586 StartY=93 StartZ=0 EndX=-108 EndY=92 EndZ=0
    g9: LineSegment StartX=-108 StartY=92 StartZ=0 EndX=-108 EndY=89 EndZ=0
    g10: LineSegment [constr] StartX=-158.75 StartY=89 StartZ=0 EndX=-108 EndY=89 EndZ=0
    g11: LineSegment StartX=-109.586 StartY=78.4894 StartZ=0 EndX=-109.586 EndY=85 EndZ=0
    g12: LineSegment StartX=-109.586 StartY=85 StartZ=0 EndX=-108 EndY=86 EndZ=0
    g13: LineSegment StartX=-108 StartY=86 StartZ=0 EndX=-108 EndY=89 EndZ=0
  constraints (30):
    c: Radius(g0) = 2.2
    c: Equal(g0,g1) = 2.2
    c: DistanceY(g1,g0) = 10.1193
    c: Equal(g0,g3) = 2.2
    c: Equal(g3,g2) = 2.2
    c: DistanceY(g2,g3) = 10.1193
    c: DistanceY(g3,g0) = 0
    c: DistanceX(g2,g3) = 0
    c: DistanceX(g3,g0) = 48.9287
    c: Coincident(g5,g6)
    c: Coincident(g6,g4)
    c: Horizontal(g4)
    c: Horizontal(g5)
    c: Vertical(g6)
    c: DistanceX(g5,g5) = 41.25
    c: DistanceY(g6,g6) = 21
    c: Coincident(g7,g4)
    c: Vertical(g7)
    c: Equal(g4,g5)
    c: Coincident(g7,g8)
    c: Coincident(g8,g9)
    c: Vertical(g9)
    c: Coincident(g10,g9)
    c: Horizontal(g10)
    c: Vertical(g11)
    c: Coincident(g11,g12)
    c: Coincident(g12,g13)
    c: Vertical(g13)
    c: Coincident(g5,g11)
    c: Coincident(g9,g13)
FEATURE [PartDesign::Pad] Pad008  label="servo_holes001"
  Length = 10
  Length2 = 100
  Placement = pos=(-260.45,178,-2) rot=(0,0,1;3.14159rad)
  Sketch = -> Sketch030
  Type = 0
FEATURE [Part::MultiFuse] Fusion009003003  label="body_without_servo_holes"
  Shapes = -> [Fusion009003002,Box001]
FEATURE [Part::MultiFuse] Fusion009003004  label="servo_holes002"
  Shapes = -> [Pad007,Pad008]
FEATURE [Part::Cut] Cut001  label="robot_futaba_body"
  Base = -> Fusion009003003
  Placement = pos=(161.5,118.9,6.5) rot=(1,0,0;3.14159rad)
  Tool = -> Fusion009003004
FEATURE [Sketcher::SketchObject] Sketch032
  Placement = pos=(161.5,118.5,63.65) rot=(0,0,1;0rad)
  sketch-geometry (4):
    g0: LineSegment StartX=-161.284 StartY=-60.5356 StartZ=0 EndX=-80.7406 EndY=-60.5356 EndZ=0
    g1: LineSegment StartX=-80.7406 StartY=-60.5356 StartZ=0 EndX=-80.7406 EndY=-116.4 EndZ=0
    g2: LineSegment StartX=-80.7406 StartY=-116.4 StartZ=0 EndX=-161.284 EndY=-116.4 EndZ=0
    g3: LineSegment StartX=-161.284 StartY=-116.4 StartZ=0 EndX=-161.284 EndY=-60.5356 EndZ=0
  constraints (8):
    c: Coincident(g0,g1)
    c: Coincident(g1,g2)
    c: Coincident(g2,g3)
    c: Coincident(g3,g0)
    c: Horizontal(g0)
    c: Horizontal(g2)
    c: Vertical(g1)
    c: Vertical(g3)
FEATURE [Part::Extrusion] Extrude
  Base = -> Sketch032
  Dir = (0,0,6.35)
  Solid = true
FEATURE [Part::Fillet] Fillet001008002
  Base = -> Extrude
  Edges = 1 edges r=1.85: [Edge12]
FEATURE [Sketcher::SketchObject] Sketch033  label="arduino_holes"
  Placement = pos=(0,0,60) rot=(0,0,1;0rad)
  sketch-geometry (4):
    g0: Circle CenterX=21.7411 CenterY=54.1491 CenterZ=0 NormalX=0 NormalY=0 NormalZ=1 Radius=1.7
    g1: Circle CenterX=20.471 CenterY=5.88126 CenterZ=0 NormalX=0 NormalY=0 NormalZ=1 Radius=1.7
    g2: Circle CenterX=72.5416 CenterY=38.9158 CenterZ=0 NormalX=0 NormalY=0 NormalZ=1 Radius=1.7
    g3: Circle CenterX=72.5535 CenterY=10.9314 CenterZ=0 NormalX=0 NormalY=0 NormalZ=1 Radius=1.7
  constraints (3):
    c: Radius(g0) = 1.7
    c: Equal(g0,g1) = 1.7
    c: Equal(g0,g2) = 1.7
FEATURE [Part::Extrusion] Extrude001
  Base = -> Sketch033
  Dir = (0,0,10)
  Placement = pos=(0,0,2) rot=(0,0,1;0rad)
  Solid = true
FEATURE [Part::MultiFuse] Fusion009003005  label="body_0"
  Shapes = -> [Cut001,Fillet001008002]
FEATURE [Part::Feature] Fusion009003005001  label="body_1"
  shape: bbox 104.1 x 59.69 x 69.85 mm, 4989 faces (baked)
FEATURE [Part::Feature] Fusion009003005001_solid  label="Fusion009003006 (Solid)"
  shape: bbox 104.1 x 59.69 x 69.85 mm, 4989 faces (baked)
FEATURE [Part::Cut] Cut002  label="robot_futaba_arduino_body"
  Base = -> Fusion009003005001_solid
  Tool = -> Extrude001
FEATURE [App::DocumentObjectGroup] Grupo029  label="old_body_sources"
  Group = -> [Fusion009003005,Fusion009003005001,Cut002]
FEATURE [Mesh::Feature] F73TK0KHZS8T535  label="gear"
  Placement = pos=(168,119,0) rot=(1,0,0;3.14159rad)
FEATURE [Mesh::Feature] FA30PZQHZS8T545  label="left_leg"
  Placement = pos=(168.5,119,0) rot=(1,0,0;3.14159rad)
FEATURE [Mesh::Feature] FHZPWI1HZS8T53I  label="right_leg"
  Placement = pos=(168.5,119,0) rot=(1,0,0;3.14159rad)
FEATURE [Mesh::Feature] FRRR7KYHZS8T54J  label="back_legs"
  Placement = pos=(35.1,186.85,4) rot=(0.92388,0.382683,0;3.14159rad)
FEATURE [Sketcher::SketchObject] Sketch035
  sketch-geometry (4):
    g0: LineSegment StartX=0 StartY=0 StartZ=0 EndX=111 EndY=0 EndZ=0
    g1: LineSegment StartX=111 StartY=0 StartZ=0 EndX=111 EndY=60 EndZ=0
    g2: LineSegment StartX=111 StartY=60 StartZ=0 EndX=0 EndY=60 EndZ=0
    g3: LineSegment StartX=0 StartY=60 StartZ=0 EndX=0 EndY=0 EndZ=0
  constraints (11):
    c: Coincident(g0,g1)
    c: Coincident(g1,g2)
    c: Coincident(g2,g3)
    c: Coincident(g3,g0)
    c: Horizontal(g0)
    c: Horizontal(g2)
    c: Vertical(g1)
    c: Vertical(g3)
    c: Coincident(g0,g-1)
    c: DistanceX(g0,g0) = 111
    c: DistanceY(g3,g3) = 60
FEATURE [PartDesign::Pad] Pad009  label="main_box"
  Length = 75
  Length2 = 100
  Sketch = -> Sketch035
  Type = 0
FEATURE [Sketcher::SketchObject] Sketch036  label="lateral_hole"
  Placement = pos=(0,0,0) rot=(1,0,0;1.5708rad)
  Support = -> Pad009 [Face1]
  sketch-geometry (4):
    g0: LineSegment StartX=9.09484 StartY=68.6505 StartZ=0 EndX=82.9846 EndY=68.6505 EndZ=0
    g1: LineSegment StartX=82.9846 StartY=68.6505 StartZ=0 EndX=82.9846 EndY=6.48725 EndZ=0
    g2: LineSegment StartX=82.9846 StartY=6.48725 StartZ=0 EndX=9.09484 EndY=6.48725 EndZ=0
    g3: LineSegment StartX=9.09484 StartY=6.48725 StartZ=0 EndX=9.09484 EndY=68.6505 EndZ=0
  constraints (11):
    c: Coincident(g0,g1)
    c: Coincident(g1,g2)
    c: Coincident(g2,g3)
    c: Coincident(g3,g0)
    c: Horizontal(g0)
    c: Horizontal(g2)
    c: Vertical(g1)
    c: Vertical(g3)
    c: DistanceX(g-1,g2) = 9.09484
    c: DistanceY(g-1,g2) = 6.48725
    c: DistanceY(g3,g3) = 62.1632
FEATURE [PartDesign::Pocket] Pocket002008007007  label="lateral_hole001"
  Length = 65
  Sketch = -> Sketch036
  Type = 0
FEATURE [Sketcher::SketchObject] Sketch037
  ExternalGeometry = -> [Pocket002008007007]
  Placement = pos=(0,0,0) rot=(0.57735,-0.57735,-0.57735;2.0944rad)
  Support = -> Pocket002008007007 [Face2]
  sketch-geometry (4):
    g0: LineSegment StartX=-56.5 StartY=68.633 StartZ=0 EndX=-3.5 EndY=68.633 EndZ=0
    g1: LineSegment StartX=-3.5 StartY=68.633 StartZ=0 EndX=-3.5 EndY=6.48725 EndZ=0
    g2: LineSegment StartX=-3.5 StartY=6.48725 StartZ=0 EndX=-56.5 EndY=6.48725 EndZ=0
    g3: LineSegment StartX=-56.5 StartY=6.48725 StartZ=0 EndX=-56.5 EndY=68.633 EndZ=0
  constraints (12):
    c: Coincident(g0,g1)
    c: Coincident(g1,g2)
    c: Coincident(g2,g3)
    c: Coincident(g3,g0)
    c: Horizontal(g0)
    c: Horizontal(g2)
    c: Vertical(g1)
    c: Vertical(g3)
    c: DistanceY(g-1,g1) = 6.48725
    c: DistanceX(g1,g-1) = 3.5
    c: DistanceX(g-3,g2) = 3.5
    c: DistanceY(g1,g1) = 62.1458
FEATURE [PartDesign::Pocket] Pocket002008007008  label="front_hole"
  Length = 10
  Sketch = -> Sketch037
  Type = 0
FEATURE [Sketcher::SketchObject] Sketch038  label="upper_hole001"
  ExternalGeometry = -> [Pocket002008007008]
  Placement = pos=(0,0,75) rot=(0,0,1;0rad)
  Support = -> Pocket002008007008 [Face4]
  sketch-geometry (4):
    g0: LineSegment StartX=91.9507 StartY=56.8266 StartZ=0 EndX=106.151 EndY=56.8266 EndZ=0
    g1: LineSegment StartX=106.151 StartY=56.8266 StartZ=0 EndX=106.151 EndY=3.1734 EndZ=0
    g2: LineSegment StartX=106.151 StartY=3.1734 StartZ=0 EndX=91.9507 EndY=3.1734 EndZ=0
    g3: LineSegment StartX=91.9507 StartY=3.1734 StartZ=0 EndX=91.9507 EndY=56.8266 EndZ=0
  constraints (13):
    c: Coincident(g0,g1)
    c: Coincident(g1,g2)
    c: Coincident(g2,g3)
    c: Coincident(g3,g0)
    c: Horizontal(g0)
    c: Horizontal(g2)
    c: Vertical(g1)
    c: Vertical(g3)
    c: DistanceY(g-3,g1) = 3.1734
    c: DistanceX(g2,g2) = 14.2
    c: DistanceY(g0,g-3) = 3.1734
    c: DistanceX(g-1,g-3) = 111
    c: DistanceX(g2,g-3) = 19.0493
FEATURE [PartDesign::Pocket] Pocket002008007009  label="upper_hole"
  Length = 90
  Sketch = -> Sketch038
  Type = 0
FEATURE [Sketcher::SketchObject] Sketch039
  ExternalGeometry = -> [Pocket002008007009]
  Placement = pos=(111,0,0) rot=(0.57735,0.57735,0.57735;2.0944rad)
  Support = -> Pocket002008007009 [Face5]
  sketch-geometry (4):
    g0: LineSegment StartX=7.04052 StartY=57.6877 StartZ=0 EndX=52.9595 EndY=57.6877 EndZ=0
    g1: LineSegment StartX=52.9595 StartY=57.6877 StartZ=0 EndX=52.9595 EndY=13.2377 EndZ=0
    g2: LineSegment StartX=52.9595 StartY=13.2377 StartZ=0 EndX=7.04052 EndY=13.2377 EndZ=0
    g3: LineSegment StartX=7.04052 StartY=13.2377 StartZ=0 EndX=7.04052 EndY=57.6877 EndZ=0
  constraints (12):
    c: Coincident(g0,g1)
    c: Coincident(g1,g2)
    c: Coincident(g2,g3)
    c: Coincident(g3,g0)
    c: Horizontal(g0)
    c: Horizontal(g2)
    c: Vertical(g1)
    c: Vertical(g3)
    c: DistanceY(g1,g1) = 44.45
    c: DistanceX(g-1,g2) = 7.04052
    c: DistanceY(g-1,g2) = 13.2377
    c: DistanceX(g1,g-3) = 7.04052
FEATURE [PartDesign::Pocket] Pocket002008007010  label="front__hole"
  Length = 15
  Sketch = -> Sketch039
  Type = 0
FEATURE [Sketcher::SketchObject] Sketch041  label="futaba_hole004"
  Placement = pos=(82,118.75,168.7) rot=(0.707107,0,0.707107;3.14159rad)
  sketch-geometry (25):
    g0: Circle CenterX=-105.746 CenterY=94.0605 CenterZ=0 NormalX=0 NormalY=0 NormalZ=1 Radius=2.2
    g1: Circle CenterX=-105.746 CenterY=83.9412 CenterZ=0 NormalX=0 NormalY=0 NormalZ=1 Radius=2.2
    g2: Circle CenterX=-154.675 CenterY=83.9412 CenterZ=0 NormalX=0 NormalY=0 NormalZ=1 Radius=2.2
    g3: Circle CenterX=-154.675 CenterY=94.0605 CenterZ=0 NormalX=0 NormalY=0 NormalZ=1 Radius=2.2
    g4: LineSegment StartX=-150.94 StartY=99.4684 StartZ=0 EndX=-109.632 EndY=99.4684 EndZ=0
    g5: LineSegment StartX=-109.647 StartY=78.4684 StartZ=0 EndX=-150.955 EndY=78.4684 EndZ=0
    g6: LineSegment StartX=-109.632 StartY=99.4684 StartZ=0 EndX=-109.632 EndY=93 EndZ=0
    g7: LineSegment StartX=-109.632 StartY=93 StartZ=0 EndX=-108 EndY=92 EndZ=0
    g8: LineSegment [constr] StartX=-158.75 StartY=89 StartZ=0 EndX=-108 EndY=89 EndZ=0
    g9: LineSegment StartX=-109.647 StartY=78.4684 StartZ=0 EndX=-109.647 EndY=85 EndZ=0
    g10: LineSegment StartX=-109.647 StartY=85 StartZ=0 EndX=-108 EndY=86 EndZ=0
    g11: LineSegment StartX=-108 StartY=86 StartZ=0 EndX=-108 EndY=87.529 EndZ=0
    g12: LineSegment StartX=-108 StartY=87.529 StartZ=0 EndX=-105.472 EndY=87.529 EndZ=0
    g13: LineSegment StartX=-108 StartY=92 StartZ=0 EndX=-108 EndY=90.4953 EndZ=0
    g14: LineSegment StartX=-108 StartY=90.4953 StartZ=0 EndX=-105.472 EndY=90.4953 EndZ=0
    g15: LineSegment StartX=-105.472 StartY=90.4953 StartZ=0 EndX=-105.472 EndY=87.529 EndZ=0
    g16: LineSegment StartX=-150.94 StartY=99.4684 StartZ=0 EndX=-150.94 EndY=93 EndZ=0
    g17: LineSegment StartX=-150.94 StartY=93 StartZ=0 EndX=-152.63 EndY=92 EndZ=0
    g18: LineSegment StartX=-152.63 StartY=90.4515 StartZ=0 EndX=-155.158 EndY=90.4515 EndZ=0
    g19: LineSegment StartX=-155.158 StartY=90.4515 StartZ=0 EndX=-155.158 EndY=87.529 EndZ=0
    g20: LineSegment StartX=-152.63 StartY=87.529 StartZ=0 EndX=-155.158 EndY=87.529 EndZ=0
    g21: LineSegment StartX=-150.955 StartY=85 StartZ=0 EndX=-152.63 EndY=86 EndZ=0
    g22: LineSegment StartX=-150.955 StartY=78.4684 StartZ=0 EndX=-150.955 EndY=85 EndZ=0
    g23: LineSegment StartX=-152.63 StartY=92 StartZ=0 EndX=-152.63 EndY=90.4515 EndZ=0
    g24: LineSegment StartX=-152.63 StartY=87.529 StartZ=0 EndX=-152.63 EndY=86 EndZ=0
  constraints (47):
    c: Radius(g0) = 2.2
    c: Equal(g0,g1) = 2.2
    c: DistanceY(g1,g0) = 10.1193
    c: Equal(g0,g3) = 2.2
    c: Equal(g3,g2) = 2.2
    c: DistanceY(g2,g3) = 10.1193
    c: DistanceY(g3,g0) = 0
    c: DistanceX(g2,g3) = 0
    c: Horizontal(g4)
    c: Horizontal(g5)
    c: DistanceY(g5,g4) = 21
    c: Coincident(g6,g4)
    c: Vertical(g6)
    c: Equal(g4,g5)
    c: Coincident(g6,g7)
    c: Horizontal(g8)
    c: Vertical(g9)
    c: Coincident(g9,g10)
    c: Coincident(g5,g9)
    c: Coincident(g11,g10)
    c: Vertical(g11)
    c: Coincident(g12,g11)
    c: Horizontal(g12)
    c: Coincident(g13,g7)
    c: Vertical(g13)
    c: Coincident(g14,g13)
    c: Horizontal(g14)
    c: Coincident(g15,g14)
    c: Coincident(g15,g12)
    c: Vertical(g15)
    c: Vertical(g16)
    c: Coincident(g16,g17)
    c: Vertical(g22)
    c: Coincident(g22,g21)
    c: Horizontal(g20)
    c: Horizontal(g18)
    c: Coincident(g19,g18)
    c: Coincident(g19,g20)
    c: Vertical(g19)
    c: Coincident(g22,g5)
    c: DistanceX(g5,g5) = 41.3077
    c: Coincident(g23,g17)
    c: Coincident(g23,g18)
    c: Vertical(g23)
    c: Coincident(g24,g20)
    c: Coincident(g24,g21)
    c: Coincident(g4,g16)
FEATURE [PartDesign::Pad] Pad010  label="futaba_hole_front"
  Length = 20
  Length2 = 100
  Placement = pos=(82,118.75,168.7) rot=(0.707107,0,0.707107;3.14159rad)
  Sketch = -> Sketch041
  Type = 0
FEATURE [Sketcher::SketchObject] Sketch042  label="futaba_hole005"
  Placement = pos=(161.4,118.75,8) rot=(1,0,0;3.14159rad)
  sketch-geometry (25):
    g0: Circle CenterX=-105.746 CenterY=94.0605 CenterZ=0 NormalX=0 NormalY=0 NormalZ=1 Radius=2.2
    g1: Circle CenterX=-105.746 CenterY=83.9412 CenterZ=0 NormalX=0 NormalY=0 NormalZ=1 Radius=2.2
    g2: Circle CenterX=-154.675 CenterY=83.9412 CenterZ=0 NormalX=0 NormalY=0 NormalZ=1 Radius=2.2
    g3: Circle CenterX=-154.675 CenterY=94.0605 CenterZ=0 NormalX=0 NormalY=0 NormalZ=1 Radius=2.2
    g4: LineSegment StartX=-150.94 StartY=99.4684 StartZ=0 EndX=-109.632 EndY=99.4684 EndZ=0
    g5: LineSegment StartX=-109.647 StartY=78.4684 StartZ=0 EndX=-150.955 EndY=78.4684 EndZ=0
    g6: LineSegment StartX=-109.632 StartY=99.4684 StartZ=0 EndX=-109.632 EndY=93 EndZ=0
    g7: LineSegment StartX=-109.632 StartY=93 StartZ=0 EndX=-108 EndY=92 EndZ=0
    g8: LineSegment [constr] StartX=-158.75 StartY=89 StartZ=0 EndX=-108 EndY=89 EndZ=0
    g9: LineSegment StartX=-109.647 StartY=78.4684 StartZ=0 EndX=-109.647 EndY=85 EndZ=0
    g10: LineSegment StartX=-109.647 StartY=85 StartZ=0 EndX=-108 EndY=86 EndZ=0
    g11: LineSegment StartX=-108 StartY=86 StartZ=0 EndX=-108 EndY=87.529 EndZ=0
    g12: LineSegment StartX=-108 StartY=87.529 StartZ=0 EndX=-105.472 EndY=87.529 EndZ=0
    g13: LineSegment StartX=-108 StartY=92 StartZ=0 EndX=-108 EndY=90.4953 EndZ=0
    g14: LineSegment StartX=-108 StartY=90.4953 StartZ=0 EndX=-105.472 EndY=90.4953 EndZ=0
    g15: LineSegment StartX=-105.472 StartY=90.4953 StartZ=0 EndX=-105.472 EndY=87.529 EndZ=0
    g16: LineSegment StartX=-150.94 StartY=99.4684 StartZ=0 EndX=-150.94 EndY=93 EndZ=0
    g17: LineSegment StartX=-150.94 StartY=93 StartZ=0 EndX=-152.63 EndY=92 EndZ=0
    g18: LineSegment StartX=-152.63 StartY=90.4515 StartZ=0 EndX=-155.158 EndY=90.4515 EndZ=0
    g19: LineSegment StartX=-155.158 StartY=90.4515 StartZ=0 EndX=-155.158 EndY=87.529 EndZ=0
    g20: LineSegment StartX=-152.63 StartY=87.529 StartZ=0 EndX=-155.158 EndY=87.529 EndZ=0
    g21: LineSegment StartX=-150.955 StartY=85 StartZ=0 EndX=-152.63 EndY=86 EndZ=0
    g22: LineSegment StartX=-150.955 StartY=78.4684 StartZ=0 EndX=-150.955 EndY=85 EndZ=0
    g23: LineSegment StartX=-152.63 StartY=92 StartZ=0 EndX=-152.63 EndY=90.4515 EndZ=0
    g24: LineSegment StartX=-152.63 StartY=87.529 StartZ=0 EndX=-152.63 EndY=86 EndZ=0
  constraints (47):
    c: Radius(g0) = 2.2
    c: Equal(g0,g1) = 2.2
    c: DistanceY(g1,g0) = 10.1193
    c: Equal(g0,g3) = 2.2
    c: Equal(g3,g2) = 2.2
    c: DistanceY(g2,g3) = 10.1193
    c: DistanceY(g3,g0) = 0
    c: DistanceX(g2,g3) = 0
    c: Horizontal(g4)
    c: Horizontal(g5)
    c: DistanceY(g5,g4) = 21
    c: Coincident(g6,g4)
    c: Vertical(g6)
    c: Equal(g4,g5)
    c: Coincident(g6,g7)
    c: Horizontal(g8)
    c: Vertical(g9)
    c: Coincident(g9,g10)
    c: Coincident(g5,g9)
    c: Coincident(g11,g10)
    c: Vertical(g11)
    c: Coincident(g12,g11)
    c: Horizontal(g12)
    c: Coincident(g13,g7)
    c: Vertical(g13)
    c: Coincident(g14,g13)
    c: Horizontal(g14)
    c: Coincident(g15,g14)
    c: Coincident(g15,g12)
    c: Vertical(g15)
    c: Vertical(g16)
    c: Coincident(g16,g17)
    c: Vertical(g22)
    c: Coincident(g22,g21)
    c: Horizontal(g20)
    c: Horizontal(g18)
    c: Coincident(g19,g18)
    c: Coincident(g19,g20)
    c: Vertical(g19)
    c: Coincident(g22,g5)
    c: DistanceX(g5,g5) = 41.3077
    c: Coincident(g23,g17)
    c: Coincident(g23,g18)
    c: Vertical(g23)
    c: Coincident(g24,g20)
    c: Coincident(g24,g21)
    c: Coincident(g4,g16)
FEATURE [PartDesign::Pad] Pad011  label="futaba_hole_bottom"
  Length = 20
  Length2 = 100
  Placement = pos=(161.4,118.75,8) rot=(1,0,0;3.14159rad)
  Sketch = -> Sketch042
  Type = 0
FEATURE [Part::Extrusion] Extrude002  label="arduino_holes001"
  Base = -> Sketch033
  Dir = (0,0,10)
  Placement = pos=(0,0,7) rot=(0,0,1;0rad)
  Solid = true
FEATURE [Sketcher::SketchObject] Sketch043  label="hidden_screw_holes"
  Placement = pos=(91.9507,0,0) rot=(0.57735,0.57735,0.57735;2.0944rad)
  Support = -> Pocket002008007010 [Face15]
  sketch-geometry (4):
    g0: Circle CenterX=24.6661 CenterY=62.9801 CenterZ=0 NormalX=0 NormalY=0 NormalZ=1 Radius=2.8
    g1: Circle CenterX=34.8021 CenterY=62.9801 CenterZ=0 NormalX=0 NormalY=0 NormalZ=1 Radius=2.8
    g2: Circle CenterX=24.6661 CenterY=13.9327 CenterZ=0 NormalX=0 NormalY=0 NormalZ=1 Radius=2.8
    g3: Circle CenterX=34.746 CenterY=13.9327 CenterZ=0 NormalX=0 NormalY=0 NormalZ=1 Radius=2.8
  constraints (10):
    c: Radius(g0) = 2.8
    c: Equal(g0,g1) = 3
    c: Equal(g0,g2) = 3
    c: Equal(g0,g3) = 3
    c: DistanceX(g0,g1) = 10.136
    c: DistanceY(g2,g0) = 49.0474
    c: DistanceX(g2,g3) = 10.0799
    c: DistanceY(g1,g0) = 0
    c: DistanceY(g2,g3) = 0
    c: DistanceX(g0,g2) = 0
FEATURE [PartDesign::Pocket] Pocket002008007011  label="body_with_screw_beds_front"
  Length = 3.5
  Sketch = -> Sketch043
  Type = 0
FEATURE [Part::MultiFuse] Fusion009003005002  label="holes_servos_and_arduino"
  Shapes = -> [Extrude002,Pad010,Pad011]
FEATURE [Part::Cut] Cut003  label="futaba_arduino_body"
  Base = -> Pocket002008007011
  Tool = -> Fusion009003005002
FEATURE [Part::Fillet] Fillet001008003  label="futaba_arduino_body001"
  Base = -> Cut003
  Edges = 12 edges r=3: [Edge1,Edge2,Edge3,Edge4,Edge9,Edge10,Edge11,Edge16,Edge17,Edge46,Edge47,Edge56]
FEATURE [App::DocumentObjectGroup] Grupo030  label="body"
  Group = -> [Pad009,Pocket002008007007,Pocket002008007008,Pocket002008007009,Pocket002008007010,Fillet001008003]
FEATURE [App::DocumentObjectGroup] Grupo031  label="sources"
  Group = -> [Compound001,Compound,Grupo027,Grupo]
FEATURE [App::DocumentObjectGroup] Grupo032  label="other_parts"
  Group = -> [F73TK0KHZS8T535,FA30PZQHZS8T545,FHZPWI1HZS8T53I,FRRR7KYHZS8T54J]
